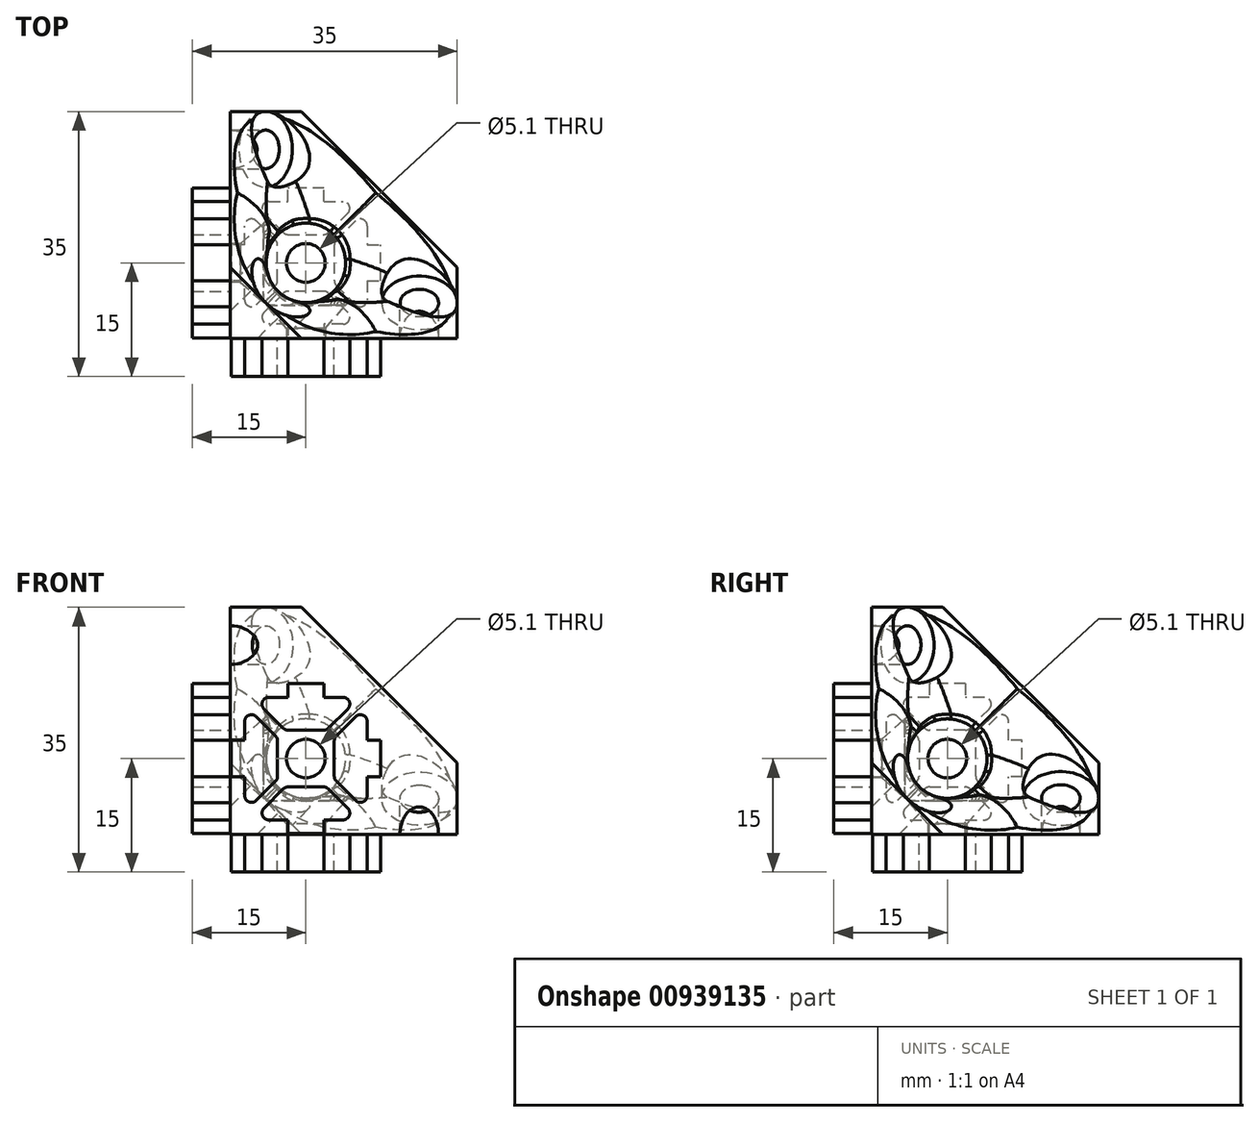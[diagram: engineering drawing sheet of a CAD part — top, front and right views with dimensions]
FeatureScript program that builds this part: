
annotation { "Feature Type Name" : "Feature", "Feature Type Description" : "" }
export const myFeature = defineFeature(function(context is Context, id is Id, definition is map)
    precondition{}
    {
        {
            var Q0;
            Q0=qCreatedBy(makeId("Front.planeOp"),FACE);
            var sketch = newSketch(context, id + "F0", { "sketchPlane" : qUnion([Q0])});
            skLineSegment(sketch, "E0.bottom", {"start": v(0, 0) * mm, "end": v(30, 0) * mm});
            skLineSegment(sketch, "E0.top", {"start": v(0, 30) * mm, "end": v(30, 30) * mm});
            skLineSegment(sketch, "E0.left", {"start": v(0, 0) * mm, "end": v(0, 30) * mm});
            skLineSegment(sketch, "E0.right", {"start": v(30, 0) * mm, "end": v(30, 30) * mm});
            skSolve(sketch);
        }
        {
            var Q0;
            Q0 = qSketchRegion(id + "F0", true);
            extrude(context, id + "F1", {"entities" : qUnion([Q0]), "oppositeDirection" : true, "depth" : 30 * mm, "offsetDistance" : 25 * mm});
        }
        {
            var Q0;
            Q0=makeQuery(id+"F1.opExtrude","CAP_FACE",FACE,{"disambiguationData":[OSD([sQuery(id+"F0.wireOp",EDGE,"E0.bottom"),sQuery(id+"F0.wireOp",EDGE,"E0.top"),sQuery(id+"F0.wireOp",EDGE,"E0.left"),sQuery(id+"F0.wireOp",EDGE,"E0.right")])],"isStart":true});
            var sketch = newSketch(context, id + "F2", { "sketchPlane" : qUnion([Q0])});
            skLineSegment(sketch, "E1", {"start": v(7.5, 20) * mm, "end": v(7.5, 18.2) * mm});
            skLineSegment(sketch, "E2", {"start": v(12.5, 20) * mm, "end": v(12.5, 18.2) * mm});
            skLineSegment(sketch, "E3", {"start": v(12.5, 18.2) * mm, "end": v(14.9, 18.2) * mm});
            skLineSegment(sketch, "E4", {"start": v(5.1, 18.2) * mm, "end": v(7.5, 18.2) * mm});
            skLineSegment(sketch, "E5", {"start": v(4.4, 16.5) * mm, "end": v(6.94, 13.94) * mm});
            skLineSegment(sketch, "E6", {"start": v(15.6, 16.5) * mm, "end": v(13.06, 13.94) * mm});
            skLineSegment(sketch, "E7", {"start": v(7.65, 13.65) * mm, "end": v(12.35, 13.65) * mm});
            skArc(sketch, "E8", {"start": v(12.35, 13.65) * mm, "mid": v(12.73, 13.73) * mm, "end": v(13.06, 13.94) * mm});
            skArc(sketch, "E9", {"start": v(6.94, 13.94) * mm, "mid": v(7.27, 13.73) * mm, "end": v(7.65, 13.65) * mm});
            skArc(sketch, "E10", {"start": v(5.1, 18.2) * mm, "mid": v(4.18, 17.58) * mm, "end": v(4.4, 16.5) * mm});
            skArc(sketch, "E11", {"start": v(15.6, 16.5) * mm, "mid": v(15.82, 17.58) * mm, "end": v(14.9, 18.2) * mm});
            skLineSegment(sketch, "E12", {"start": v(7.5, 20) * mm, "end": v(12.5, 20) * mm});
            skLineSegment(sketch, "E13.0", {"start": v(9.41, 30) * mm, "end": v(30, 9.41) * mm, "construction": true});
            skLineSegment(sketch, "E14", {"start": v(0, 30) * mm, "end": v(9.41, 30) * mm, "construction": true});
            skLineSegment(sketch, "E15", {"start": v(30, 0) * mm, "end": v(30, 9.41) * mm, "construction": true});
            skLineSegment(sketch, "E16.0", {"start": v(7.6, 19.9) * mm, "end": v(7.6, 18.1) * mm});
            skLineSegment(sketch, "E16.1", {"start": v(15.54, 16.56) * mm, "end": v(12.99, 14.01) * mm});
            skArc(sketch, "E16.2", {"start": v(15.54, 16.56) * mm, "mid": v(15.73, 17.54) * mm, "end": v(14.9, 18.1) * mm});
            skLineSegment(sketch, "E16.3", {"start": v(12.4, 18.1) * mm, "end": v(14.9, 18.1) * mm});
            skLineSegment(sketch, "E16.4", {"start": v(12.4, 19.9) * mm, "end": v(12.4, 18.1) * mm});
            skArc(sketch, "E16.5", {"start": v(12.35, 13.75) * mm, "mid": v(12.7, 13.82) * mm, "end": v(12.99, 14.01) * mm});
            skLineSegment(sketch, "E16.6", {"start": v(7.6, 19.9) * mm, "end": v(12.4, 19.9) * mm});
            skLineSegment(sketch, "E16.7", {"start": v(7.65, 13.75) * mm, "end": v(12.35, 13.75) * mm});
            skArc(sketch, "E16.8", {"start": v(7.01, 14.01) * mm, "mid": v(7.3, 13.82) * mm, "end": v(7.65, 13.75) * mm});
            skLineSegment(sketch, "E16.9", {"start": v(4.46, 16.56) * mm, "end": v(7.01, 14.01) * mm});
            skArc(sketch, "E16.10", {"start": v(5.1, 18.1) * mm, "mid": v(4.27, 17.54) * mm, "end": v(4.46, 16.56) * mm});
            skLineSegment(sketch, "E16.11", {"start": v(5.1, 18.1) * mm, "end": v(7.6, 18.1) * mm});
            skLineSegment(sketch, "E17.1.0", {"start": v(0.1, 7.6) * mm, "end": v(0.1, 12.4) * mm});
            skLineSegment(sketch, "E17.1.1", {"start": v(0.1, 7.6) * mm, "end": v(1.9, 7.6) * mm});
            skLineSegment(sketch, "E17.1.2", {"start": v(1.9, 5.1) * mm, "end": v(1.9, 7.6) * mm});
            skArc(sketch, "E17.1.3", {"start": v(1.9, 5.1) * mm, "mid": v(2.46, 4.27) * mm, "end": v(3.44, 4.46) * mm});
            skLineSegment(sketch, "E17.1.4", {"start": v(3.44, 4.46) * mm, "end": v(5.99, 7.01) * mm});
            skArc(sketch, "E17.1.5", {"start": v(5.99, 7.01) * mm, "mid": v(6.18, 7.3) * mm, "end": v(6.25, 7.65) * mm});
            skLineSegment(sketch, "E17.1.6", {"start": v(6.25, 7.65) * mm, "end": v(6.25, 12.35) * mm});
            skArc(sketch, "E17.1.7", {"start": v(6.25, 12.35) * mm, "mid": v(6.18, 12.7) * mm, "end": v(5.99, 12.99) * mm});
            skLineSegment(sketch, "E17.1.8", {"start": v(3.44, 15.54) * mm, "end": v(5.99, 12.99) * mm});
            skArc(sketch, "E17.1.9", {"start": v(3.44, 15.54) * mm, "mid": v(2.46, 15.73) * mm, "end": v(1.9, 14.9) * mm});
            skLineSegment(sketch, "E17.1.10", {"start": v(1.9, 12.4) * mm, "end": v(1.9, 14.9) * mm});
            skLineSegment(sketch, "E17.1.11", {"start": v(0.1, 12.4) * mm, "end": v(1.9, 12.4) * mm});
            skLineSegment(sketch, "E17.2.0", {"start": v(12.4, 0.1) * mm, "end": v(7.6, 0.1) * mm});
            skLineSegment(sketch, "E17.2.1", {"start": v(12.4, 0.1) * mm, "end": v(12.4, 1.9) * mm});
            skLineSegment(sketch, "E17.2.2", {"start": v(14.9, 1.9) * mm, "end": v(12.4, 1.9) * mm});
            skArc(sketch, "E17.2.3", {"start": v(14.9, 1.9) * mm, "mid": v(15.73, 2.46) * mm, "end": v(15.54, 3.44) * mm});
            skLineSegment(sketch, "E17.2.4", {"start": v(15.54, 3.44) * mm, "end": v(12.99, 5.99) * mm});
            skArc(sketch, "E17.2.5", {"start": v(12.99, 5.99) * mm, "mid": v(12.7, 6.18) * mm, "end": v(12.35, 6.25) * mm});
            skLineSegment(sketch, "E17.2.6", {"start": v(12.35, 6.25) * mm, "end": v(7.65, 6.25) * mm});
            skArc(sketch, "E17.2.7", {"start": v(7.65, 6.25) * mm, "mid": v(7.3, 6.18) * mm, "end": v(7.01, 5.99) * mm});
            skLineSegment(sketch, "E17.2.8", {"start": v(4.46, 3.44) * mm, "end": v(7.01, 5.99) * mm});
            skArc(sketch, "E17.2.9", {"start": v(4.46, 3.44) * mm, "mid": v(4.27, 2.46) * mm, "end": v(5.1, 1.9) * mm});
            skLineSegment(sketch, "E17.2.10", {"start": v(7.6, 1.9) * mm, "end": v(5.1, 1.9) * mm});
            skLineSegment(sketch, "E17.2.11", {"start": v(7.6, 0.1) * mm, "end": v(7.6, 1.9) * mm});
            skLineSegment(sketch, "E17.3.0", {"start": v(19.9, 12.4) * mm, "end": v(19.9, 7.6) * mm});
            skLineSegment(sketch, "E17.3.1", {"start": v(19.9, 12.4) * mm, "end": v(18.1, 12.4) * mm});
            skLineSegment(sketch, "E17.3.2", {"start": v(18.1, 14.9) * mm, "end": v(18.1, 12.4) * mm});
            skArc(sketch, "E17.3.3", {"start": v(18.1, 14.9) * mm, "mid": v(17.54, 15.73) * mm, "end": v(16.56, 15.54) * mm});
            skLineSegment(sketch, "E17.3.4", {"start": v(16.56, 15.54) * mm, "end": v(14.01, 12.99) * mm});
            skArc(sketch, "E17.3.5", {"start": v(14.01, 12.99) * mm, "mid": v(13.82, 12.7) * mm, "end": v(13.75, 12.35) * mm});
            skLineSegment(sketch, "E17.3.6", {"start": v(13.75, 12.35) * mm, "end": v(13.75, 7.65) * mm});
            skArc(sketch, "E17.3.7", {"start": v(13.75, 7.65) * mm, "mid": v(13.82, 7.3) * mm, "end": v(14.01, 7.01) * mm});
            skLineSegment(sketch, "E17.3.8", {"start": v(16.56, 4.46) * mm, "end": v(14.01, 7.01) * mm});
            skArc(sketch, "E17.3.9", {"start": v(16.56, 4.46) * mm, "mid": v(17.54, 4.27) * mm, "end": v(18.1, 5.1) * mm});
            skLineSegment(sketch, "E17.3.10", {"start": v(18.1, 7.6) * mm, "end": v(18.1, 5.1) * mm});
            skLineSegment(sketch, "E17.3.11", {"start": v(19.9, 7.6) * mm, "end": v(18.1, 7.6) * mm});
            skPoint(sketch, "E17.center", {"position": v(10, 10) * mm});
            skCircle(sketch, "E18", {"center": v(10, 10) * mm, "radius": 2.55 * mm});
            skLineSegment(sketch, "E19", {"start": v(0, 0) * mm, "end": v(0, 9.41) * mm, "construction": true});
            skLineSegment(sketch, "E20", {"start": v(0, 9.41) * mm, "end": v(9.41, 0.1) * mm, "construction": true});
            skLineSegment(sketch, "E21", {"start": v(9.41, 0.1) * mm, "end": v(0, 0) * mm, "construction": true});
            skSolve(sketch);
        }
        {
            var Q0;
            Q0=makeQuery(id+"F2.imprint","IMPRINT",FACE,{"disambiguationData":[TD([[makeQuery(id+"F2.imprint","IMPRINT",EDGE,{"derivedFrom":sQuery(id+"F2.wireOp",EDGE,"E16.0")}),1.0]])]});
            var Q1;
            Q1=makeQuery(id+"F2.imprint","IMPRINT",FACE,{"disambiguationData":[TD([[makeQuery(id+"F2.imprint","IMPRINT",EDGE,{"derivedFrom":sQuery(id+"F2.wireOp",EDGE,"E17.1.0")}),-1.0]])]});
            var Q2;
            Q2=makeQuery(id+"F2.imprint","IMPRINT",FACE,{"disambiguationData":[TD([[makeQuery(id+"F2.imprint","IMPRINT",EDGE,{"derivedFrom":sQuery(id+"F2.wireOp",EDGE,"E17.3.0")}),-1.0]])]});
            var Q3;
            Q3=makeQuery(id+"F2.imprint","IMPRINT",FACE,{"disambiguationData":[TD([[makeQuery(id+"F2.imprint","IMPRINT",EDGE,{"derivedFrom":sQuery(id+"F2.wireOp",EDGE,"E17.2.0")}),-1.0]])]});
            extrude(context, id + "F3", {"entities" : qUnion([Q0, Q1, Q2, Q3]), "operationType" : NewBodyOperationType.ADD, "depth" : 5 * mm, "offsetDistance" : 25 * mm});
        }
        {
            var Q0;
            Q0=makeQuery(id+"F2.imprint","IMPRINT",FACE,{"disambiguationData":[TD([[makeQuery(id+"F2.imprint","IMPRINT",EDGE,{"derivedFrom":sQuery(id+"F2.wireOp",EDGE,"E18")}),1.0]])]});
            extrude(context, id + "F4", {"entities" : qUnion([Q0]), "operationType" : NewBodyOperationType.REMOVE, "oppositeDirection" : true, "depth" : 1.35 * mm, "offsetDistance" : 25 * mm});
        }
        {
            var Q0;
            Q0=qCreatedBy(makeId("Front.planeOp"),FACE);
            cPlane(context, id + "F5", {"entities" : qUnion([Q0]), "cplaneType" : CPlaneType.OFFSET, "offset" : 4.4 * mm, "oppositeDirection" : true, "width" : 150 * mm, "height" : 150 * mm});
        }
        {
            var Q0;
            Q0=qCreatedBy(id+"F5.planeOp",FACE);
            var sketch = newSketch(context, id + "F6", { "sketchPlane" : qUnion([Q0])});
            skCircle(sketch, "E22", {"center": v(10, 10) * mm, "radius": 5.25 * mm});
            skSolve(sketch);
        }
        {
            var Q0;
            Q0 = qSketchRegion(id + "F6", true);
            extrude(context, id + "F7", {"entities" : qUnion([Q0]), "operationType" : NewBodyOperationType.REMOVE, "endBound" : BoundingType.THROUGH_ALL, "oppositeDirection" : true, "depth" : 25 * mm, "offsetDistance" : 25 * mm});
        }
        {
            var Q1;
            Q1=makeQuery(id+"F7.boolean.opBoolean","COPY",FACE,{"derivedFrom":makeQuery(id+"F7.opExtrude","CAP_FACE",FACE,{"disambiguationData":[OSD([sQuery(id+"F6.wireOp",EDGE,"E22")])],"isStart":true})});
            var Q2;
            Q2=makeQuery(id+"F4.boolean.opBoolean","COPY",FACE,{"derivedFrom":makeQuery(id+"F4.opExtrude","CAP_FACE",FACE,{"disambiguationData":[OSD([sQuery(id+"F2.wireOp",EDGE,"E18")])],"isStart":false})});
            loft(context, id + "F8", {"operationType" : NewBodyOperationType.REMOVE, "sheetProfilesArray" : [{ "sheetProfileEntities" : qUnion([Q1]) }, { "sheetProfileEntities" : qUnion([Q2]) }]});
        }
        {
            var Q0;
            Q0=makeQuery(id+"F1.opExtrude","SWEPT_FACE",FACE,{"disambiguationData":[OSD([sQuery(id+"F0.wireOp",EDGE,"E0.left")])]});
            var sketch = newSketch(context, id + "F9", { "sketchPlane" : qUnion([Q0])});
            skLineSegment(sketch, "E23.0", {"start": v(-9.41, 30) * mm, "end": v(-30, 9.41) * mm, "construction": true});
            skLineSegment(sketch, "E24", {"start": v(0, 30) * mm, "end": v(-9.41, 30) * mm, "construction": true});
            skLineSegment(sketch, "E25", {"start": v(-30, 9.41) * mm, "end": v(-30, 0) * mm, "construction": true});
            skCircle(sketch, "E26", {"center": v(-10, 10) * mm, "radius": 2.55 * mm});
            skLineSegment(sketch, "E27", {"start": v(0, 0) * mm, "end": v(-9.41, 0) * mm, "construction": true});
            skPoint(sketch, "E27.endSnap0", {"position": v(-9.41, 0.1) * mm});
            skLineSegment(sketch, "E28", {"start": v(-9.41, 0) * mm, "end": v(-0.09, 9.41) * mm, "construction": true});
            skLineSegment(sketch, "E29", {"start": v(-0.09, 9.41) * mm, "end": v(0, 0) * mm, "construction": true});
            skLineSegment(sketch, "E30", {"start": v(-12.5, 20) * mm, "end": v(-12.5, 18.2) * mm});
            skLineSegment(sketch, "E31", {"start": v(-7.5, 20) * mm, "end": v(-7.5, 18.2) * mm});
            skLineSegment(sketch, "E32", {"start": v(-7.5, 18.2) * mm, "end": v(-5.1, 18.2) * mm});
            skLineSegment(sketch, "E33", {"start": v(-14.9, 18.2) * mm, "end": v(-12.5, 18.2) * mm});
            skLineSegment(sketch, "E34", {"start": v(-15.6, 16.5) * mm, "end": v(-13.06, 13.94) * mm});
            skLineSegment(sketch, "E35", {"start": v(-4.4, 16.5) * mm, "end": v(-6.94, 13.94) * mm});
            skLineSegment(sketch, "E36", {"start": v(-12.35, 13.65) * mm, "end": v(-7.65, 13.65) * mm});
            skArc(sketch, "E37", {"start": v(-7.65, 13.65) * mm, "mid": v(-7.27, 13.73) * mm, "end": v(-6.94, 13.94) * mm});
            skArc(sketch, "E38", {"start": v(-13.06, 13.94) * mm, "mid": v(-12.73, 13.73) * mm, "end": v(-12.35, 13.65) * mm});
            skArc(sketch, "E39", {"start": v(-14.9, 18.2) * mm, "mid": v(-15.82, 17.58) * mm, "end": v(-15.6, 16.5) * mm});
            skArc(sketch, "E40", {"start": v(-4.4, 16.5) * mm, "mid": v(-4.18, 17.58) * mm, "end": v(-5.1, 18.2) * mm});
            skLineSegment(sketch, "E41", {"start": v(-12.5, 20) * mm, "end": v(-7.5, 20) * mm});
            skLineSegment(sketch, "E42.0", {"start": v(-12.4, 19.9) * mm, "end": v(-12.4, 18.1) * mm});
            skLineSegment(sketch, "E42.1", {"start": v(-4.46, 16.56) * mm, "end": v(-7.01, 14.01) * mm});
            skArc(sketch, "E42.2", {"start": v(-4.46, 16.56) * mm, "mid": v(-4.27, 17.54) * mm, "end": v(-5.1, 18.1) * mm});
            skLineSegment(sketch, "E42.3", {"start": v(-7.6, 18.1) * mm, "end": v(-5.1, 18.1) * mm});
            skLineSegment(sketch, "E42.4", {"start": v(-7.6, 19.9) * mm, "end": v(-7.6, 18.1) * mm});
            skArc(sketch, "E42.5", {"start": v(-7.65, 13.75) * mm, "mid": v(-7.3, 13.82) * mm, "end": v(-7.01, 14.01) * mm});
            skLineSegment(sketch, "E42.6", {"start": v(-12.4, 19.9) * mm, "end": v(-7.6, 19.9) * mm});
            skLineSegment(sketch, "E42.7", {"start": v(-12.35, 13.75) * mm, "end": v(-7.65, 13.75) * mm});
            skArc(sketch, "E42.8", {"start": v(-12.99, 14.01) * mm, "mid": v(-12.7, 13.82) * mm, "end": v(-12.35, 13.75) * mm});
            skLineSegment(sketch, "E42.9", {"start": v(-15.54, 16.56) * mm, "end": v(-12.99, 14.01) * mm});
            skArc(sketch, "E42.10", {"start": v(-14.9, 18.1) * mm, "mid": v(-15.73, 17.54) * mm, "end": v(-15.54, 16.56) * mm});
            skLineSegment(sketch, "E42.11", {"start": v(-14.9, 18.1) * mm, "end": v(-12.4, 18.1) * mm});
            skLineSegment(sketch, "E43.1.0", {"start": v(-19.9, 7.6) * mm, "end": v(-19.9, 12.4) * mm});
            skLineSegment(sketch, "E43.1.1", {"start": v(-19.9, 7.6) * mm, "end": v(-18.1, 7.6) * mm});
            skLineSegment(sketch, "E43.1.2", {"start": v(-18.1, 5.1) * mm, "end": v(-18.1, 7.6) * mm});
            skArc(sketch, "E43.1.3", {"start": v(-18.1, 5.1) * mm, "mid": v(-17.54, 4.27) * mm, "end": v(-16.56, 4.46) * mm});
            skLineSegment(sketch, "E43.1.4", {"start": v(-16.56, 4.46) * mm, "end": v(-14.01, 7.01) * mm});
            skArc(sketch, "E43.1.5", {"start": v(-14.01, 7.01) * mm, "mid": v(-13.82, 7.3) * mm, "end": v(-13.75, 7.65) * mm});
            skLineSegment(sketch, "E43.1.6", {"start": v(-13.75, 7.65) * mm, "end": v(-13.75, 12.35) * mm});
            skArc(sketch, "E43.1.7", {"start": v(-13.75, 12.35) * mm, "mid": v(-13.82, 12.7) * mm, "end": v(-14.01, 12.99) * mm});
            skLineSegment(sketch, "E43.1.8", {"start": v(-16.56, 15.54) * mm, "end": v(-14.01, 12.99) * mm});
            skArc(sketch, "E43.1.9", {"start": v(-16.56, 15.54) * mm, "mid": v(-17.54, 15.73) * mm, "end": v(-18.1, 14.9) * mm});
            skLineSegment(sketch, "E43.1.10", {"start": v(-18.1, 12.4) * mm, "end": v(-18.1, 14.9) * mm});
            skLineSegment(sketch, "E43.1.11", {"start": v(-19.9, 12.4) * mm, "end": v(-18.1, 12.4) * mm});
            skLineSegment(sketch, "E43.2.0", {"start": v(-7.6, 0.1) * mm, "end": v(-12.4, 0.1) * mm});
            skLineSegment(sketch, "E43.2.1", {"start": v(-7.6, 0.1) * mm, "end": v(-7.6, 1.9) * mm});
            skLineSegment(sketch, "E43.2.2", {"start": v(-5.1, 1.9) * mm, "end": v(-7.6, 1.9) * mm});
            skArc(sketch, "E43.2.3", {"start": v(-5.1, 1.9) * mm, "mid": v(-4.27, 2.46) * mm, "end": v(-4.46, 3.44) * mm});
            skLineSegment(sketch, "E43.2.4", {"start": v(-4.46, 3.44) * mm, "end": v(-7.01, 5.99) * mm});
            skArc(sketch, "E43.2.5", {"start": v(-7.01, 5.99) * mm, "mid": v(-7.3, 6.18) * mm, "end": v(-7.65, 6.25) * mm});
            skLineSegment(sketch, "E43.2.6", {"start": v(-7.65, 6.25) * mm, "end": v(-12.35, 6.25) * mm});
            skArc(sketch, "E43.2.7", {"start": v(-12.35, 6.25) * mm, "mid": v(-12.7, 6.18) * mm, "end": v(-12.99, 5.99) * mm});
            skLineSegment(sketch, "E43.2.8", {"start": v(-15.54, 3.44) * mm, "end": v(-12.99, 5.99) * mm});
            skArc(sketch, "E43.2.9", {"start": v(-15.54, 3.44) * mm, "mid": v(-15.73, 2.46) * mm, "end": v(-14.9, 1.9) * mm});
            skLineSegment(sketch, "E43.2.10", {"start": v(-12.4, 1.9) * mm, "end": v(-14.9, 1.9) * mm});
            skLineSegment(sketch, "E43.2.11", {"start": v(-12.4, 0.1) * mm, "end": v(-12.4, 1.9) * mm});
            skLineSegment(sketch, "E43.3.0", {"start": v(-0.1, 12.4) * mm, "end": v(-0.1, 7.6) * mm});
            skLineSegment(sketch, "E43.3.1", {"start": v(-0.1, 12.4) * mm, "end": v(-1.9, 12.4) * mm});
            skLineSegment(sketch, "E43.3.2", {"start": v(-1.9, 14.9) * mm, "end": v(-1.9, 12.4) * mm});
            skArc(sketch, "E43.3.3", {"start": v(-1.9, 14.9) * mm, "mid": v(-2.46, 15.73) * mm, "end": v(-3.44, 15.54) * mm});
            skLineSegment(sketch, "E43.3.4", {"start": v(-3.44, 15.54) * mm, "end": v(-5.99, 12.99) * mm});
            skArc(sketch, "E43.3.5", {"start": v(-5.99, 12.99) * mm, "mid": v(-6.18, 12.7) * mm, "end": v(-6.25, 12.35) * mm});
            skLineSegment(sketch, "E43.3.6", {"start": v(-6.25, 12.35) * mm, "end": v(-6.25, 7.65) * mm});
            skArc(sketch, "E43.3.7", {"start": v(-6.25, 7.65) * mm, "mid": v(-6.18, 7.3) * mm, "end": v(-5.99, 7.01) * mm});
            skLineSegment(sketch, "E43.3.8", {"start": v(-3.44, 4.46) * mm, "end": v(-5.99, 7.01) * mm});
            skArc(sketch, "E43.3.9", {"start": v(-3.44, 4.46) * mm, "mid": v(-2.46, 4.27) * mm, "end": v(-1.9, 5.1) * mm});
            skLineSegment(sketch, "E43.3.10", {"start": v(-1.9, 7.6) * mm, "end": v(-1.9, 5.1) * mm});
            skLineSegment(sketch, "E43.3.11", {"start": v(-0.1, 7.6) * mm, "end": v(-1.9, 7.6) * mm});
            skSolve(sketch);
        }
        {
            var Q0;
            Q0=makeQuery(id+"F9.imprint","IMPRINT",FACE,{"disambiguationData":[TD([[makeQuery(id+"F9.imprint","IMPRINT",EDGE,{"derivedFrom":sQuery(id+"F9.wireOp",EDGE,"E42.0")}),1.0]])]});
            var Q1;
            Q1=makeQuery(id+"F9.imprint","IMPRINT",FACE,{"disambiguationData":[TD([[makeQuery(id+"F9.imprint","IMPRINT",EDGE,{"derivedFrom":sQuery(id+"F9.wireOp",EDGE,"E43.1.0")}),-1.0]])]});
            var Q2;
            Q2=makeQuery(id+"F9.imprint","IMPRINT",FACE,{"disambiguationData":[TD([[makeQuery(id+"F9.imprint","IMPRINT",EDGE,{"derivedFrom":sQuery(id+"F9.wireOp",EDGE,"E43.2.0")}),-1.0]])]});
            var Q3;
            Q3=makeQuery(id+"F9.imprint","IMPRINT",FACE,{"disambiguationData":[TD([[makeQuery(id+"F9.imprint","IMPRINT",EDGE,{"derivedFrom":sQuery(id+"F9.wireOp",EDGE,"E43.3.0")}),-1.0]])]});
            extrude(context, id + "F10", {"entities" : qUnion([Q0, Q1, Q2, Q3]), "operationType" : NewBodyOperationType.ADD, "depth" : 5 * mm, "offsetDistance" : 25 * mm});
        }
        {
            var Q0;
            Q0=makeQuery(id+"F9.imprint","IMPRINT",FACE,{"disambiguationData":[TD([[makeQuery(id+"F9.imprint","IMPRINT",EDGE,{"derivedFrom":sQuery(id+"F9.wireOp",EDGE,"E26")}),1.0]])]});
            extrude(context, id + "F11", {"entities" : qUnion([Q0]), "operationType" : NewBodyOperationType.REMOVE, "oppositeDirection" : true, "depth" : 1.35 * mm, "offsetDistance" : 25 * mm});
        }
        {
            var Q0;
            Q0=qCreatedBy(makeId("Right.planeOp"),FACE);
            cPlane(context, id + "F12", {"entities" : qUnion([Q0]), "cplaneType" : CPlaneType.OFFSET, "offset" : 4.4 * mm, "width" : 150 * mm, "height" : 150 * mm});
        }
        {
            var Q0;
            Q0=qCreatedBy(id+"F12.planeOp",FACE);
            var sketch = newSketch(context, id + "F13", { "sketchPlane" : qUnion([Q0])});
            skCircle(sketch, "E44", {"center": v(10, 10) * mm, "radius": 5.25 * mm});
            skSolve(sketch);
        }
        {
            var Q0;
            Q0 = qSketchRegion(id + "F13", true);
            var Q1;
            Q1=makeQuery(id+"F1.opExtrude","SWEPT_FACE",FACE,{"disambiguationData":[OSD([sQuery(id+"F0.wireOp",EDGE,"E0.right")])]});
            extrude(context, id + "F14", {"entities" : qUnion([Q0]), "operationType" : NewBodyOperationType.REMOVE, "endBound" : BoundingType.UP_TO_SURFACE, "depth" : 25 * mm, "endBoundEntityFace" : qUnion([Q1]), "offsetDistance" : 25 * mm});
        }
        {
            var Q1;
            Q1=makeQuery(id+"F11.boolean.opBoolean","COPY",FACE,{"derivedFrom":makeQuery(id+"F11.opExtrude","CAP_FACE",FACE,{"disambiguationData":[OSD([sQuery(id+"F9.wireOp",EDGE,"E26")])],"isStart":false})});
            var Q2;
            Q2=makeQuery(id+"F14.boolean.opBoolean","COPY",FACE,{"derivedFrom":makeQuery(id+"F14.opExtrude","CAP_FACE",FACE,{"disambiguationData":[OSD([sQuery(id+"F13.wireOp",EDGE,"E44")])],"isStart":true})});
            loft(context, id + "F15", {"operationType" : NewBodyOperationType.REMOVE, "sheetProfilesArray" : [{ "sheetProfileEntities" : qUnion([Q1]) }, { "sheetProfileEntities" : qUnion([Q2]) }]});
        }
        {
            var Q0;
            Q0=makeQuery(id+"F1.opExtrude","SWEPT_FACE",FACE,{"disambiguationData":[OSD([sQuery(id+"F0.wireOp",EDGE,"E0.bottom")])]});
            var sketch = newSketch(context, id + "F16", { "sketchPlane" : qUnion([Q0])});
            skLineSegment(sketch, "E45", {"start": v(18.2, -7.5) * mm, "end": v(20, -7.5) * mm});
            skLineSegment(sketch, "E46", {"start": v(18.2, -12.5) * mm, "end": v(20, -12.5) * mm});
            skLineSegment(sketch, "E47", {"start": v(18.2, -14.9) * mm, "end": v(18.2, -12.5) * mm});
            skLineSegment(sketch, "E48", {"start": v(18.2, -7.5) * mm, "end": v(18.2, -5.1) * mm});
            skLineSegment(sketch, "E49", {"start": v(13.94, -13.06) * mm, "end": v(16.5, -15.6) * mm});
            skLineSegment(sketch, "E50", {"start": v(13.94, -6.94) * mm, "end": v(16.5, -4.4) * mm});
            skLineSegment(sketch, "E51", {"start": v(13.65, -12.35) * mm, "end": v(13.65, -7.65) * mm});
            skArc(sketch, "E52", {"start": v(13.65, -12.35) * mm, "mid": v(13.73, -12.73) * mm, "end": v(13.94, -13.06) * mm});
            skArc(sketch, "E53", {"start": v(13.94, -6.94) * mm, "mid": v(13.73, -7.27) * mm, "end": v(13.65, -7.65) * mm});
            skArc(sketch, "E54", {"start": v(18.2, -5.1) * mm, "mid": v(17.58, -4.18) * mm, "end": v(16.5, -4.4) * mm});
            skArc(sketch, "E55", {"start": v(16.5, -15.6) * mm, "mid": v(17.58, -15.82) * mm, "end": v(18.2, -14.9) * mm});
            skLineSegment(sketch, "E56", {"start": v(20, -7.5) * mm, "end": v(20, -12.5) * mm});
            skLineSegment(sketch, "E57.0", {"start": v(9.41, -30) * mm, "end": v(30, -9.41) * mm, "construction": true});
            skLineSegment(sketch, "E58", {"start": v(30, 0) * mm, "end": v(30, -30) * mm, "construction": true});
            skLineSegment(sketch, "E59", {"start": v(30, -30) * mm, "end": v(0, -30) * mm, "construction": true});
            skCircle(sketch, "E60", {"center": v(10, -10) * mm, "radius": 2.55 * mm});
            skLineSegment(sketch, "E61.0", {"start": v(18.1, -7.6) * mm, "end": v(19.9, -7.6) * mm});
            skLineSegment(sketch, "E61.1", {"start": v(14.01, -12.99) * mm, "end": v(16.56, -15.54) * mm});
            skArc(sketch, "E61.2", {"start": v(16.56, -15.54) * mm, "mid": v(17.54, -15.73) * mm, "end": v(18.1, -14.9) * mm});
            skLineSegment(sketch, "E61.3", {"start": v(18.1, -14.9) * mm, "end": v(18.1, -12.4) * mm});
            skLineSegment(sketch, "E61.4", {"start": v(18.1, -12.4) * mm, "end": v(19.9, -12.4) * mm});
            skArc(sketch, "E61.5", {"start": v(13.75, -12.35) * mm, "mid": v(13.82, -12.7) * mm, "end": v(14.01, -12.99) * mm});
            skLineSegment(sketch, "E61.6", {"start": v(19.9, -7.6) * mm, "end": v(19.9, -12.4) * mm});
            skLineSegment(sketch, "E61.7", {"start": v(13.75, -12.35) * mm, "end": v(13.75, -7.65) * mm});
            skArc(sketch, "E61.8", {"start": v(14.01, -7.01) * mm, "mid": v(13.82, -7.3) * mm, "end": v(13.75, -7.65) * mm});
            skLineSegment(sketch, "E61.9", {"start": v(14.01, -7.01) * mm, "end": v(16.56, -4.46) * mm});
            skArc(sketch, "E61.10", {"start": v(18.1, -5.1) * mm, "mid": v(17.54, -4.27) * mm, "end": v(16.56, -4.46) * mm});
            skLineSegment(sketch, "E61.11", {"start": v(18.1, -7.6) * mm, "end": v(18.1, -5.1) * mm});
            skLineSegment(sketch, "E62.1.0", {"start": v(7.6, -0.1) * mm, "end": v(12.4, -0.1) * mm});
            skLineSegment(sketch, "E62.1.1", {"start": v(7.6, -1.9) * mm, "end": v(7.6, -0.1) * mm});
            skLineSegment(sketch, "E62.1.2", {"start": v(7.6, -1.9) * mm, "end": v(5.1, -1.9) * mm});
            skArc(sketch, "E62.1.3", {"start": v(5.1, -1.9) * mm, "mid": v(4.27, -2.46) * mm, "end": v(4.46, -3.44) * mm});
            skLineSegment(sketch, "E62.1.4", {"start": v(7.01, -5.99) * mm, "end": v(4.46, -3.44) * mm});
            skArc(sketch, "E62.1.5", {"start": v(7.01, -5.99) * mm, "mid": v(7.3, -6.18) * mm, "end": v(7.65, -6.25) * mm});
            skLineSegment(sketch, "E62.1.6", {"start": v(12.35, -6.25) * mm, "end": v(7.65, -6.25) * mm});
            skArc(sketch, "E62.1.7", {"start": v(12.35, -6.25) * mm, "mid": v(12.7, -6.18) * mm, "end": v(12.99, -5.99) * mm});
            skLineSegment(sketch, "E62.1.8", {"start": v(12.99, -5.99) * mm, "end": v(15.54, -3.44) * mm});
            skArc(sketch, "E62.1.9", {"start": v(15.54, -3.44) * mm, "mid": v(15.73, -2.46) * mm, "end": v(14.9, -1.9) * mm});
            skLineSegment(sketch, "E62.1.10", {"start": v(14.9, -1.9) * mm, "end": v(12.4, -1.9) * mm});
            skLineSegment(sketch, "E62.1.11", {"start": v(12.4, -1.9) * mm, "end": v(12.4, -0.1) * mm});
            skLineSegment(sketch, "E62.2.0", {"start": v(0.1, -12.4) * mm, "end": v(0.1, -7.6) * mm});
            skLineSegment(sketch, "E62.2.1", {"start": v(1.9, -12.4) * mm, "end": v(0.1, -12.4) * mm});
            skLineSegment(sketch, "E62.2.2", {"start": v(1.9, -12.4) * mm, "end": v(1.9, -14.9) * mm});
            skArc(sketch, "E62.2.3", {"start": v(1.9, -14.9) * mm, "mid": v(2.46, -15.73) * mm, "end": v(3.44, -15.54) * mm});
            skLineSegment(sketch, "E62.2.4", {"start": v(5.99, -12.99) * mm, "end": v(3.44, -15.54) * mm});
            skArc(sketch, "E62.2.5", {"start": v(5.99, -12.99) * mm, "mid": v(6.18, -12.7) * mm, "end": v(6.25, -12.35) * mm});
            skLineSegment(sketch, "E62.2.6", {"start": v(6.25, -7.65) * mm, "end": v(6.25, -12.35) * mm});
            skArc(sketch, "E62.2.7", {"start": v(6.25, -7.65) * mm, "mid": v(6.18, -7.3) * mm, "end": v(5.99, -7.01) * mm});
            skLineSegment(sketch, "E62.2.8", {"start": v(5.99, -7.01) * mm, "end": v(3.44, -4.46) * mm});
            skArc(sketch, "E62.2.9", {"start": v(3.44, -4.46) * mm, "mid": v(2.46, -4.27) * mm, "end": v(1.9, -5.1) * mm});
            skLineSegment(sketch, "E62.2.10", {"start": v(1.9, -5.1) * mm, "end": v(1.9, -7.6) * mm});
            skLineSegment(sketch, "E62.2.11", {"start": v(1.9, -7.6) * mm, "end": v(0.1, -7.6) * mm});
            skLineSegment(sketch, "E62.3.0", {"start": v(12.4, -19.9) * mm, "end": v(7.6, -19.9) * mm});
            skLineSegment(sketch, "E62.3.1", {"start": v(12.4, -18.1) * mm, "end": v(12.4, -19.9) * mm});
            skLineSegment(sketch, "E62.3.2", {"start": v(12.4, -18.1) * mm, "end": v(14.9, -18.1) * mm});
            skArc(sketch, "E62.3.3", {"start": v(14.9, -18.1) * mm, "mid": v(15.73, -17.54) * mm, "end": v(15.54, -16.56) * mm});
            skLineSegment(sketch, "E62.3.4", {"start": v(12.99, -14.01) * mm, "end": v(15.54, -16.56) * mm});
            skArc(sketch, "E62.3.5", {"start": v(12.99, -14.01) * mm, "mid": v(12.7, -13.82) * mm, "end": v(12.35, -13.75) * mm});
            skLineSegment(sketch, "E62.3.6", {"start": v(7.65, -13.75) * mm, "end": v(12.35, -13.75) * mm});
            skArc(sketch, "E62.3.7", {"start": v(7.65, -13.75) * mm, "mid": v(7.3, -13.82) * mm, "end": v(7.01, -14.01) * mm});
            skLineSegment(sketch, "E62.3.8", {"start": v(7.01, -14.01) * mm, "end": v(4.46, -16.56) * mm});
            skArc(sketch, "E62.3.9", {"start": v(4.46, -16.56) * mm, "mid": v(4.27, -17.54) * mm, "end": v(5.1, -18.1) * mm});
            skLineSegment(sketch, "E62.3.10", {"start": v(5.1, -18.1) * mm, "end": v(7.6, -18.1) * mm});
            skLineSegment(sketch, "E62.3.11", {"start": v(7.6, -18.1) * mm, "end": v(7.6, -19.9) * mm});
            skPoint(sketch, "E63", {"position": v(9.41, 0) * mm});
            skSolve(sketch);
        }
        {
            var Q0;
            Q0=makeQuery(id+"F16.imprint","IMPRINT",FACE,{"disambiguationData":[TD([[makeQuery(id+"F16.imprint","IMPRINT",EDGE,{"derivedFrom":sQuery(id+"F16.wireOp",EDGE,"E61.0")}),-1.0]])]});
            var Q1;
            Q1=makeQuery(id+"F16.imprint","IMPRINT",FACE,{"disambiguationData":[TD([[makeQuery(id+"F16.imprint","IMPRINT",EDGE,{"derivedFrom":sQuery(id+"F16.wireOp",EDGE,"E62.1.0")}),-1.0]])]});
            var Q2;
            Q2=makeQuery(id+"F16.imprint","IMPRINT",FACE,{"disambiguationData":[TD([[makeQuery(id+"F16.imprint","IMPRINT",EDGE,{"derivedFrom":sQuery(id+"F16.wireOp",EDGE,"E62.3.0")}),-1.0]])]});
            var Q3;
            Q3=makeQuery(id+"F16.imprint","IMPRINT",FACE,{"disambiguationData":[TD([[makeQuery(id+"F16.imprint","IMPRINT",EDGE,{"derivedFrom":sQuery(id+"F16.wireOp",EDGE,"E62.2.0")}),-1.0]])]});
            extrude(context, id + "F17", {"entities" : qUnion([Q0, Q1, Q2, Q3]), "operationType" : NewBodyOperationType.ADD, "depth" : 5 * mm, "offsetDistance" : 25 * mm});
        }
        {
            var Q0;
            Q0=makeQuery(id+"F16.imprint","IMPRINT",FACE,{"disambiguationData":[TD([[makeQuery(id+"F16.imprint","IMPRINT",EDGE,{"derivedFrom":sQuery(id+"F16.wireOp",EDGE,"E60")}),1.0]])]});
            extrude(context, id + "F18", {"entities" : qUnion([Q0]), "operationType" : NewBodyOperationType.REMOVE, "oppositeDirection" : true, "depth" : 1.35 * mm, "offsetDistance" : 25 * mm});
        }
        {
            var Q0;
            Q0=qCreatedBy(makeId("Top.planeOp"),FACE);
            cPlane(context, id + "F19", {"entities" : qUnion([Q0]), "cplaneType" : CPlaneType.OFFSET, "offset" : 4.4 * mm, "width" : 150 * mm, "height" : 150 * mm});
        }
        {
            var Q0;
            Q0=qCreatedBy(id+"F19.planeOp",FACE);
            var sketch = newSketch(context, id + "F20", { "sketchPlane" : qUnion([Q0])});
            skCircle(sketch, "E64", {"center": v(10, 10) * mm, "radius": 5.25 * mm});
            skSolve(sketch);
        }
        {
            var Q0;
            Q0 = qSketchRegion(id + "F20", true);
            var Q1;
            Q1=makeQuery(id+"F1.opExtrude","SWEPT_FACE",FACE,{"disambiguationData":[OSD([sQuery(id+"F0.wireOp",EDGE,"E0.top")])]});
            extrude(context, id + "F21", {"entities" : qUnion([Q0]), "operationType" : NewBodyOperationType.REMOVE, "endBound" : BoundingType.UP_TO_SURFACE, "depth" : 25 * mm, "endBoundEntityFace" : qUnion([Q1]), "offsetDistance" : 25 * mm});
        }
        {
            var Q1;
            Q1=makeQuery(id+"F18.boolean.opBoolean","COPY",FACE,{"derivedFrom":makeQuery(id+"F18.opExtrude","CAP_FACE",FACE,{"disambiguationData":[OSD([sQuery(id+"F16.wireOp",EDGE,"E60")])],"isStart":false})});
            var Q2;
            Q2=makeQuery(id+"F21.boolean.opBoolean","COPY",FACE,{"derivedFrom":makeQuery(id+"F21.opExtrude","CAP_FACE",FACE,{"disambiguationData":[OSD([sQuery(id+"F20.wireOp",EDGE,"E64")])],"isStart":true})});
            loft(context, id + "F22", {"operationType" : NewBodyOperationType.REMOVE, "sheetProfilesArray" : [{ "sheetProfileEntities" : qUnion([Q1]) }, { "sheetProfileEntities" : qUnion([Q2]) }]});
        }
        {
            var Q0;
            Q0=sQuery(id+"F2.wireOp",VERTEX,"E13.0.start");
            var Q1;
            Q1=sQuery(id+"F9.wireOp",VERTEX,"E23.0.start");
            var Q2;
            Q2=sQuery(id+"F9.wireOp",VERTEX,"E23.0.end");
            cPlane(context, id + "F23", {"entities" : qUnion([Q0, Q1, Q2]), "cplaneType" : CPlaneType.THREE_POINT, "offset" : 25 * mm, "width" : 150 * mm, "height" : 150 * mm});
        }
        {
            var Q0;
            Q0=qCreatedBy(id+"F23.planeOp",FACE);
            var sketch = newSketch(context, id + "F24", { "sketchPlane" : qUnion([Q0])});
            skLineSegment(sketch, "E65", {"start": v(4.56, 21.21) * mm, "end": v(16.1, 14.56) * mm});
            skLineSegment(sketch, "E66", {"start": v(16.1, 14.56) * mm, "end": v(16.1, -14.56) * mm});
            skLineSegment(sketch, "E67", {"start": v(16.1, -14.56) * mm, "end": v(4.56, -21.21) * mm});
            skLineSegment(sketch, "E68", {"start": v(4.56, -21.21) * mm, "end": v(-20.65, -6.66) * mm});
            skLineSegment(sketch, "E69", {"start": v(-20.65, -6.66) * mm, "end": v(-20.65, 6.66) * mm});
            skLineSegment(sketch, "E70", {"start": v(-20.65, 6.66) * mm, "end": v(4.56, 21.21) * mm});
            skSolve(sketch);
        }
        {
            var Q0;
            Q0 = qSketchRegion(id + "F24", true);
            var Q1;
            Q1=makeQuery(id+"F1.opExtrude","CAP_VERTEX",VERTEX,{"disambiguationData":[OSD([sQuery(id+"F0.wireOp",EDGE,"E0.top"),sQuery(id+"F0.wireOp",EDGE,"E0.right")])],"isStart":false});
            extrude(context, id + "F25", {"entities" : qUnion([Q0]), "operationType" : NewBodyOperationType.REMOVE, "endBound" : BoundingType.UP_TO_VERTEX, "depth" : 25 * mm, "endBoundEntityVertex" : qUnion([Q1]), "offsetDistance" : 25 * mm});
        }
        {
            var Q0;
            Q0=makeQuery(id+"F25.boolean.opBoolean","COPY",FACE,{"derivedFrom":makeQuery(id+"F25.opExtrude","SWEPT_FACE",FACE,{"disambiguationData":[OSD([sQuery(id+"F24.wireOp",EDGE,"E70")])]})});
            var Q1;
            Q1=makeQuery(id+"F1.opExtrude","CAP_VERTEX",VERTEX,{"disambiguationData":[OSD([sQuery(id+"F0.wireOp",EDGE,"E0.top"),sQuery(id+"F0.wireOp",EDGE,"E0.right")])],"isStart":true});
            extrude(context, id + "F26", {"entities" : qUnion([Q0]), "operationType" : NewBodyOperationType.REMOVE, "endBound" : BoundingType.UP_TO_VERTEX, "oppositeDirection" : true, "depth" : 25 * mm, "endBoundEntityVertex" : qUnion([Q1]), "offsetDistance" : 25 * mm});
        }
        {
            var Q0;
            Q0=makeQuery(id+"F25.boolean.opBoolean","COPY",FACE,{"derivedFrom":makeQuery(id+"F25.opExtrude","SWEPT_FACE",FACE,{"disambiguationData":[OSD([sQuery(id+"F24.wireOp",EDGE,"E66")])]})});
            var Q1;
            Q1=makeQuery(id+"F1.opExtrude","CAP_VERTEX",VERTEX,{"disambiguationData":[OSD([sQuery(id+"F0.wireOp",EDGE,"E0.top"),sQuery(id+"F0.wireOp",EDGE,"E0.left")])],"isStart":false});
            extrude(context, id + "F27", {"entities" : qUnion([Q0]), "operationType" : NewBodyOperationType.REMOVE, "endBound" : BoundingType.UP_TO_VERTEX, "oppositeDirection" : true, "depth" : 25 * mm, "endBoundEntityVertex" : qUnion([Q1]), "offsetDistance" : 25 * mm});
        }
        {
            var Q0;
            Q0=makeQuery(id+"F25.boolean.opBoolean","COPY",FACE,{"derivedFrom":makeQuery(id+"F25.opExtrude","SWEPT_FACE",FACE,{"disambiguationData":[OSD([sQuery(id+"F24.wireOp",EDGE,"E68")])]})});
            var Q1;
            Q1=sQuery(id+"F16.wireOp",VERTEX,"E58.end");
            extrude(context, id + "F28", {"entities" : qUnion([Q0]), "operationType" : NewBodyOperationType.REMOVE, "endBound" : BoundingType.UP_TO_VERTEX, "oppositeDirection" : true, "depth" : 25 * mm, "endBoundEntityVertex" : qUnion([Q1]), "offsetDistance" : 25 * mm});
        }
        {
            var Q0;
            Q0=sQuery(id+"F2.wireOp",VERTEX,"E19.end");
            var Q1;
            {var subQ1=sQuery(id+"F24.wireOp",EDGE,"E67");var subQ2=sQuery(id+"F24.wireOp",EDGE,"E66");Q1=makeQuery(id+"F25.boolean.opBoolean","COPY",VERTEX,{"disambiguationData":[TD([makeQuery(id+"F25.opExtrude","CAP_FACE",FACE,{"disambiguationData":[OSD([sQuery(id+"F24.wireOp",EDGE,"E65"),subQ2,subQ1,sQuery(id+"F24.wireOp",EDGE,"E68"),sQuery(id+"F24.wireOp",EDGE,"E69"),sQuery(id+"F24.wireOp",EDGE,"E70")])],"isStart":true})])],"derivedFrom":makeQuery(id+"F25.opExtrude","CAP_VERTEX",VERTEX,{"disambiguationData":[OSD([subQ2,subQ1])],"isStart":true})});}
            var Q2;
            {var subQ1=sQuery(id+"F24.wireOp",EDGE,"E68");var subQ2=sQuery(id+"F24.wireOp",EDGE,"E67");Q2=makeQuery(id+"F25.boolean.opBoolean","COPY",VERTEX,{"disambiguationData":[TD([makeQuery(id+"F25.opExtrude","CAP_FACE",FACE,{"disambiguationData":[OSD([sQuery(id+"F24.wireOp",EDGE,"E65"),sQuery(id+"F24.wireOp",EDGE,"E66"),subQ2,subQ1,sQuery(id+"F24.wireOp",EDGE,"E69"),sQuery(id+"F24.wireOp",EDGE,"E70")])],"isStart":true})])],"derivedFrom":makeQuery(id+"F25.opExtrude","CAP_VERTEX",VERTEX,{"disambiguationData":[OSD([subQ2,subQ1])],"isStart":true})});}
            cPlane(context, id + "F29", {"entities" : qUnion([Q0, Q1, Q2]), "cplaneType" : CPlaneType.THREE_POINT, "offset" : 25 * mm, "width" : 150 * mm, "height" : 150 * mm});
        }
        {
            var Q0;
            Q0=qCreatedBy(id+"F29.planeOp",FACE);
            var sketch = newSketch(context, id + "F30", { "sketchPlane" : qUnion([Q0])});
            skCircle(sketch, "E71", {"center": v(-0.05, 25) * mm, "radius": 2.55 * mm});
            skSolve(sketch);
        }
        {
            var Q0;
            Q0 = qSketchRegion(id + "F30", true);
            var Q1;
            Q1=makeQuery(id+"F1.opExtrude","CAP_VERTEX",VERTEX,{"disambiguationData":[OSD([sQuery(id+"F0.wireOp",EDGE,"E0.bottom"),sQuery(id+"F0.wireOp",EDGE,"E0.left")])],"isStart":false});
            extrude(context, id + "F31", {"entities" : qUnion([Q0]), "operationType" : NewBodyOperationType.REMOVE, "endBound" : BoundingType.UP_TO_VERTEX, "oppositeDirection" : true, "depth" : 25 * mm, "endBoundEntityVertex" : qUnion([Q1]), "offsetDistance" : 25 * mm});
        }
        {
            var Q0;
            Q0=qCreatedBy(id+"F29.planeOp",FACE);
            var sketch = newSketch(context, id + "F32", { "sketchPlane" : qUnion([Q0])});
            skCircle(sketch, "E72", {"center": v(-0.05, 25) * mm, "radius": 5 * mm});
            skSolve(sketch);
        }
        {
            var Q0;
            Q0 = qSketchRegion(id + "F32", true);
            var Q1;
            Q1=makeQuery(id+"F21.boolean.opBoolean","SPLIT",FACE,{"disambiguationData":[TD([makeQuery(id+"F1.opExtrude","CAP_FACE",FACE,{"disambiguationData":[OSD([sQuery(id+"F0.wireOp",EDGE,"E0.bottom"),sQuery(id+"F0.wireOp",EDGE,"E0.top"),sQuery(id+"F0.wireOp",EDGE,"E0.left"),sQuery(id+"F0.wireOp",EDGE,"E0.right")])],"isStart":false})])],"derivedFrom":makeQuery(id+"F7.boolean.opBoolean","COPY",FACE,{"derivedFrom":makeQuery(id+"F7.opExtrude","SWEPT_FACE",FACE,{"disambiguationData":[OSD([sQuery(id+"F6.wireOp",EDGE,"E22")])]})})});
            extrude(context, id + "F33", {"entities" : qUnion([Q0]), "operationType" : NewBodyOperationType.REMOVE, "endBound" : BoundingType.UP_TO_SURFACE, "depth" : 25 * mm, "endBoundEntityFace" : qUnion([Q1]), "offsetDistance" : 25 * mm});
        }
        {
            var Q0;
            Q0=sQuery(id+"F9.wireOp",VERTEX,"E27.endSnap0");
            var Q1;
            {var subQ0=sQuery(id+"F24.wireOp",EDGE,"E69");var subQ1=sQuery(id+"F24.wireOp",EDGE,"E68");Q1=makeQuery(id+"F25.boolean.opBoolean","COPY",VERTEX,{"disambiguationData":[TD([makeQuery(id+"F25.opExtrude","CAP_FACE",FACE,{"disambiguationData":[OSD([sQuery(id+"F24.wireOp",EDGE,"E65"),sQuery(id+"F24.wireOp",EDGE,"E66"),sQuery(id+"F24.wireOp",EDGE,"E67"),subQ1,subQ0,sQuery(id+"F24.wireOp",EDGE,"E70")])],"isStart":true})])],"derivedFrom":makeQuery(id+"F25.opExtrude","CAP_VERTEX",VERTEX,{"disambiguationData":[OSD([subQ1,subQ0])],"isStart":true})});}
            var Q2;
            {var subQ1=sQuery(id+"F24.wireOp",EDGE,"E70");var subQ2=sQuery(id+"F24.wireOp",EDGE,"E69");Q2=makeQuery(id+"F25.boolean.opBoolean","COPY",VERTEX,{"disambiguationData":[TD([makeQuery(id+"F25.opExtrude","CAP_FACE",FACE,{"disambiguationData":[OSD([sQuery(id+"F24.wireOp",EDGE,"E65"),sQuery(id+"F24.wireOp",EDGE,"E66"),sQuery(id+"F24.wireOp",EDGE,"E67"),sQuery(id+"F24.wireOp",EDGE,"E68"),subQ2,subQ1])],"isStart":true})])],"derivedFrom":makeQuery(id+"F25.opExtrude","CAP_VERTEX",VERTEX,{"disambiguationData":[OSD([subQ2,subQ1])],"isStart":true})});}
            cPlane(context, id + "F34", {"entities" : qUnion([Q0, Q1, Q2]), "cplaneType" : CPlaneType.THREE_POINT, "offset" : 25 * mm, "width" : 150 * mm, "height" : 150 * mm});
        }
        {
            var Q0;
            Q0=qCreatedBy(id+"F34.planeOp",FACE);
            var sketch = newSketch(context, id + "F35", { "sketchPlane" : qUnion([Q0])});
            skCircle(sketch, "E73", {"center": v(-24.98, 0) * mm, "radius": 2.55 * mm});
            skSolve(sketch);
        }
        {
            var Q0;
            Q0 = qSketchRegion(id + "F35", true);
            var Q1;
            Q1=makeQuery(id+"F1.opExtrude","CAP_VERTEX",VERTEX,{"disambiguationData":[OSD([sQuery(id+"F0.wireOp",EDGE,"E0.bottom"),sQuery(id+"F0.wireOp",EDGE,"E0.right")])],"isStart":true});
            extrude(context, id + "F36", {"entities" : qUnion([Q0]), "operationType" : NewBodyOperationType.REMOVE, "endBound" : BoundingType.UP_TO_VERTEX, "oppositeDirection" : true, "depth" : 25 * mm, "endBoundEntityVertex" : qUnion([Q1]), "offsetDistance" : 25 * mm});
        }
        {
            var Q0;
            Q0=qCreatedBy(id+"F34.planeOp",FACE);
            var sketch = newSketch(context, id + "F37", { "sketchPlane" : qUnion([Q0])});
            skCircle(sketch, "E74", {"center": v(-24.98, 0) * mm, "radius": 5 * mm});
            skSolve(sketch);
        }
        {
            var Q0;
            Q0 = qSketchRegion(id + "F37", true);
            extrude(context, id + "F38", {"entities" : qUnion([Q0]), "operationType" : NewBodyOperationType.REMOVE, "depth" : 25 * mm, "offsetDistance" : 25 * mm});
        }
        {
            var Q0;
            Q0=sQuery(id+"F16.wireOp",VERTEX,"E63");
            var Q1;
            {var subQ1=sQuery(id+"F24.wireOp",EDGE,"E70");var subQ2=sQuery(id+"F24.wireOp",EDGE,"E65");Q1=makeQuery(id+"F25.boolean.opBoolean","COPY",VERTEX,{"disambiguationData":[TD([makeQuery(id+"F25.opExtrude","CAP_FACE",FACE,{"disambiguationData":[OSD([subQ2,sQuery(id+"F24.wireOp",EDGE,"E66"),sQuery(id+"F24.wireOp",EDGE,"E67"),sQuery(id+"F24.wireOp",EDGE,"E68"),sQuery(id+"F24.wireOp",EDGE,"E69"),subQ1])],"isStart":true})])],"derivedFrom":makeQuery(id+"F25.opExtrude","CAP_VERTEX",VERTEX,{"disambiguationData":[OSD([subQ2,subQ1])],"isStart":true})});}
            var Q2;
            {var subQ0=sQuery(id+"F24.wireOp",EDGE,"E66");var subQ1=sQuery(id+"F24.wireOp",EDGE,"E65");Q2=makeQuery(id+"F25.boolean.opBoolean","COPY",VERTEX,{"disambiguationData":[TD([makeQuery(id+"F25.opExtrude","CAP_FACE",FACE,{"disambiguationData":[OSD([subQ1,subQ0,sQuery(id+"F24.wireOp",EDGE,"E67"),sQuery(id+"F24.wireOp",EDGE,"E68"),sQuery(id+"F24.wireOp",EDGE,"E69"),sQuery(id+"F24.wireOp",EDGE,"E70")])],"isStart":true})])],"derivedFrom":makeQuery(id+"F25.opExtrude","CAP_VERTEX",VERTEX,{"disambiguationData":[OSD([subQ1,subQ0])],"isStart":true})});}
            cPlane(context, id + "F39", {"entities" : qUnion([Q0, Q1, Q2]), "cplaneType" : CPlaneType.THREE_POINT, "offset" : 25 * mm, "width" : 150 * mm, "height" : 150 * mm});
        }
        {
            var Q0;
            Q0=qCreatedBy(id+"F39.planeOp",FACE);
            var sketch = newSketch(context, id + "F40", { "sketchPlane" : qUnion([Q0])});
            skCircle(sketch, "E75", {"center": v(0, 25) * mm, "radius": 2.55 * mm});
            skSolve(sketch);
        }
        {
            var Q0;
            Q0 = qSketchRegion(id + "F40", true);
            var Q1;
            Q1=makeQuery(id+"F1.opExtrude","CAP_VERTEX",VERTEX,{"disambiguationData":[OSD([sQuery(id+"F0.wireOp",EDGE,"E0.top"),sQuery(id+"F0.wireOp",EDGE,"E0.left")])],"isStart":true});
            extrude(context, id + "F41", {"entities" : qUnion([Q0]), "operationType" : NewBodyOperationType.REMOVE, "endBound" : BoundingType.UP_TO_VERTEX, "oppositeDirection" : true, "depth" : 25 * mm, "endBoundEntityVertex" : qUnion([Q1]), "offsetDistance" : 25 * mm});
        }
        {
            var Q0;
            Q0=qCreatedBy(id+"F39.planeOp",FACE);
            var sketch = newSketch(context, id + "F42", { "sketchPlane" : qUnion([Q0])});
            skCircle(sketch, "E76", {"center": v(0, 25) * mm, "radius": 5 * mm});
            skSolve(sketch);
        }
        {
            var Q0;
            Q0 = qSketchRegion(id + "F42", true);
            extrude(context, id + "F43", {"entities" : qUnion([Q0]), "operationType" : NewBodyOperationType.REMOVE, "depth" : 7.4 * mm, "offsetDistance" : 25 * mm});
        }
        {
            var Q0;
            {var subQ0=makeQuery(id+"F7.boolean.opBoolean","COPY",FACE,{"derivedFrom":makeQuery(id+"F7.opExtrude","SWEPT_FACE",FACE,{"disambiguationData":[OSD([sQuery(id+"F6.wireOp",EDGE,"E22")])]})});var subQ1=sQuery(id+"F0.wireOp",EDGE,"E0.top");var subQ3=makeQuery(id+"F21.opExtrude","SWEPT_FACE",FACE,{"disambiguationData":[OSD([sQuery(id+"F20.wireOp",EDGE,"E64")])]});var subQ4=makeQuery(id+"F25.opExtrude","CAP_FACE",FACE,{"disambiguationData":[OSD([sQuery(id+"F24.wireOp",EDGE,"E65"),sQuery(id+"F24.wireOp",EDGE,"E66"),sQuery(id+"F24.wireOp",EDGE,"E67"),sQuery(id+"F24.wireOp",EDGE,"E68"),sQuery(id+"F24.wireOp",EDGE,"E69"),sQuery(id+"F24.wireOp",EDGE,"E70")])],"isStart":true});Q0=makeQuery(id+"F33.boolean.opBoolean","SPLIT",EDGE,{"disambiguationData":[TD([makeQuery(id+"F21.boolean.opBoolean","COPY",FACE,{"disambiguationData":[TD([makeQuery(id+"F1.opExtrude","SWEPT_FACE",FACE,{"disambiguationData":[OSD([subQ1])]})])],"derivedFrom":subQ3})])],"derivedFrom":makeQuery(id+"F25.boolean.opBoolean","INTERSECT",EDGE,{"derivedFrom":[makeQuery(id+"F21.boolean.opBoolean","SPLIT",FACE,{"disambiguationData":[TD([makeQuery(id+"F1.opExtrude","CAP_FACE",FACE,{"disambiguationData":[OSD([sQuery(id+"F0.wireOp",EDGE,"E0.bottom"),subQ1,sQuery(id+"F0.wireOp",EDGE,"E0.left"),sQuery(id+"F0.wireOp",EDGE,"E0.right")])],"isStart":false})])],"derivedFrom":subQ0}),subQ4]})});}
            var Q1;
            {var subQ0=makeQuery(id+"F7.boolean.opBoolean","COPY",FACE,{"derivedFrom":makeQuery(id+"F7.opExtrude","SWEPT_FACE",FACE,{"disambiguationData":[OSD([sQuery(id+"F6.wireOp",EDGE,"E22")])]})});var subQ1=makeQuery(id+"F21.boolean.opBoolean","COPY",FACE,{"disambiguationData":[TD([makeQuery(id+"F1.opExtrude","SWEPT_FACE",FACE,{"disambiguationData":[OSD([sQuery(id+"F0.wireOp",EDGE,"E0.top")])]})])],"derivedFrom":makeQuery(id+"F21.opExtrude","SWEPT_FACE",FACE,{"disambiguationData":[OSD([sQuery(id+"F20.wireOp",EDGE,"E64")])]})});var subQ2=makeQuery(id+"F25.opExtrude","CAP_FACE",FACE,{"disambiguationData":[OSD([sQuery(id+"F24.wireOp",EDGE,"E65"),sQuery(id+"F24.wireOp",EDGE,"E66"),sQuery(id+"F24.wireOp",EDGE,"E67"),sQuery(id+"F24.wireOp",EDGE,"E68"),sQuery(id+"F24.wireOp",EDGE,"E69"),sQuery(id+"F24.wireOp",EDGE,"E70")])],"isStart":true});Q1=makeQuery(id+"F43.boolean.opBoolean","SPLIT",EDGE,{"disambiguationData":[TD([subQ0])],"derivedFrom":makeQuery(id+"F25.boolean.opBoolean","INTERSECT",EDGE,{"derivedFrom":[subQ1,subQ2]})});}
            var Q2;
            {var subQ0=makeQuery(id+"F14.boolean.opBoolean","COPY",FACE,{"derivedFrom":makeQuery(id+"F14.opExtrude","SWEPT_FACE",FACE,{"disambiguationData":[OSD([sQuery(id+"F13.wireOp",EDGE,"E44")])]})});var subQ1=makeQuery(id+"F21.boolean.opBoolean","COPY",FACE,{"disambiguationData":[TD([makeQuery(id+"F1.opExtrude","SWEPT_FACE",FACE,{"disambiguationData":[OSD([sQuery(id+"F0.wireOp",EDGE,"E0.top")])]})])],"derivedFrom":makeQuery(id+"F21.opExtrude","SWEPT_FACE",FACE,{"disambiguationData":[OSD([sQuery(id+"F20.wireOp",EDGE,"E64")])]})});var subQ2=makeQuery(id+"F25.opExtrude","CAP_FACE",FACE,{"disambiguationData":[OSD([sQuery(id+"F24.wireOp",EDGE,"E65"),sQuery(id+"F24.wireOp",EDGE,"E66"),sQuery(id+"F24.wireOp",EDGE,"E67"),sQuery(id+"F24.wireOp",EDGE,"E68"),sQuery(id+"F24.wireOp",EDGE,"E69"),sQuery(id+"F24.wireOp",EDGE,"E70")])],"isStart":true});Q2=makeQuery(id+"F43.boolean.opBoolean","SPLIT",EDGE,{"disambiguationData":[TD([subQ0])],"derivedFrom":makeQuery(id+"F25.boolean.opBoolean","INTERSECT",EDGE,{"derivedFrom":[subQ1,subQ2]})});}
            var Q3;
            {var subQ0=makeQuery(id+"F14.boolean.opBoolean","COPY",FACE,{"derivedFrom":makeQuery(id+"F14.opExtrude","SWEPT_FACE",FACE,{"disambiguationData":[OSD([sQuery(id+"F13.wireOp",EDGE,"E44")])]})});var subQ2=makeQuery(id+"F21.opExtrude","SWEPT_FACE",FACE,{"disambiguationData":[OSD([sQuery(id+"F20.wireOp",EDGE,"E64")])]});var subQ3=makeQuery(id+"F25.opExtrude","CAP_FACE",FACE,{"disambiguationData":[OSD([sQuery(id+"F24.wireOp",EDGE,"E65"),sQuery(id+"F24.wireOp",EDGE,"E66"),sQuery(id+"F24.wireOp",EDGE,"E67"),sQuery(id+"F24.wireOp",EDGE,"E68"),sQuery(id+"F24.wireOp",EDGE,"E69"),sQuery(id+"F24.wireOp",EDGE,"E70")])],"isStart":true});Q3=makeQuery(id+"F38.boolean.opBoolean","SPLIT",EDGE,{"disambiguationData":[TD([makeQuery(id+"F21.boolean.opBoolean","COPY",FACE,{"disambiguationData":[TD([makeQuery(id+"F1.opExtrude","SWEPT_FACE",FACE,{"disambiguationData":[OSD([sQuery(id+"F0.wireOp",EDGE,"E0.top")])]})])],"derivedFrom":subQ2})])],"derivedFrom":makeQuery(id+"F25.boolean.opBoolean","INTERSECT",EDGE,{"derivedFrom":[makeQuery(id+"F21.boolean.opBoolean","SPLIT",FACE,{"disambiguationData":[TD([makeQuery(id+"F1.opExtrude","SWEPT_FACE",FACE,{"disambiguationData":[OSD([sQuery(id+"F0.wireOp",EDGE,"E0.right")])]})])],"derivedFrom":subQ0}),subQ3]})});}
            var Q4;
            {var subQ0=makeQuery(id+"F7.boolean.opBoolean","COPY",FACE,{"derivedFrom":makeQuery(id+"F7.opExtrude","SWEPT_FACE",FACE,{"disambiguationData":[OSD([sQuery(id+"F6.wireOp",EDGE,"E22")])]})});var subQ1=makeQuery(id+"F14.boolean.opBoolean","COPY",FACE,{"derivedFrom":makeQuery(id+"F14.opExtrude","SWEPT_FACE",FACE,{"disambiguationData":[OSD([sQuery(id+"F13.wireOp",EDGE,"E44")])]})});var subQ2=makeQuery(id+"F25.opExtrude","CAP_FACE",FACE,{"disambiguationData":[OSD([sQuery(id+"F24.wireOp",EDGE,"E65"),sQuery(id+"F24.wireOp",EDGE,"E66"),sQuery(id+"F24.wireOp",EDGE,"E67"),sQuery(id+"F24.wireOp",EDGE,"E68"),sQuery(id+"F24.wireOp",EDGE,"E69"),sQuery(id+"F24.wireOp",EDGE,"E70")])],"isStart":true});Q4=makeQuery(id+"F38.boolean.opBoolean","SPLIT",EDGE,{"disambiguationData":[TD([subQ0])],"derivedFrom":makeQuery(id+"F25.boolean.opBoolean","INTERSECT",EDGE,{"derivedFrom":[makeQuery(id+"F21.boolean.opBoolean","SPLIT",FACE,{"disambiguationData":[TD([makeQuery(id+"F1.opExtrude","SWEPT_FACE",FACE,{"disambiguationData":[OSD([sQuery(id+"F0.wireOp",EDGE,"E0.right")])]})])],"derivedFrom":subQ1}),subQ2]})});}
            var Q5;
            {var subQ0=makeQuery(id+"F7.boolean.opBoolean","COPY",FACE,{"derivedFrom":makeQuery(id+"F7.opExtrude","SWEPT_FACE",FACE,{"disambiguationData":[OSD([sQuery(id+"F6.wireOp",EDGE,"E22")])]})});var subQ1=makeQuery(id+"F14.boolean.opBoolean","COPY",FACE,{"derivedFrom":makeQuery(id+"F14.opExtrude","SWEPT_FACE",FACE,{"disambiguationData":[OSD([sQuery(id+"F13.wireOp",EDGE,"E44")])]})});var subQ2=makeQuery(id+"F25.opExtrude","CAP_FACE",FACE,{"disambiguationData":[OSD([sQuery(id+"F24.wireOp",EDGE,"E65"),sQuery(id+"F24.wireOp",EDGE,"E66"),sQuery(id+"F24.wireOp",EDGE,"E67"),sQuery(id+"F24.wireOp",EDGE,"E68"),sQuery(id+"F24.wireOp",EDGE,"E69"),sQuery(id+"F24.wireOp",EDGE,"E70")])],"isStart":true});Q5=makeQuery(id+"F33.boolean.opBoolean","SPLIT",EDGE,{"disambiguationData":[TD([subQ1])],"derivedFrom":makeQuery(id+"F25.boolean.opBoolean","INTERSECT",EDGE,{"derivedFrom":[makeQuery(id+"F21.boolean.opBoolean","SPLIT",FACE,{"disambiguationData":[TD([makeQuery(id+"F1.opExtrude","CAP_FACE",FACE,{"disambiguationData":[OSD([sQuery(id+"F0.wireOp",EDGE,"E0.bottom"),sQuery(id+"F0.wireOp",EDGE,"E0.top"),sQuery(id+"F0.wireOp",EDGE,"E0.left"),sQuery(id+"F0.wireOp",EDGE,"E0.right")])],"isStart":false})])],"derivedFrom":subQ0}),subQ2]})});}
            fillet(context, id + "F44", {"entities" : qUnion([Q0, Q1, Q2, Q3, Q4, Q5]), "radius" : 10 * mm, "tangentPropagation" : true});
        }
        {
            var Q0;
            {var subQ0=makeQuery(id+"F7.boolean.opBoolean","COPY",FACE,{"derivedFrom":makeQuery(id+"F7.opExtrude","SWEPT_FACE",FACE,{"disambiguationData":[OSD([sQuery(id+"F6.wireOp",EDGE,"E22")])]})});var subQ1=sQuery(id+"F13.wireOp",EDGE,"E44");var subQ2=makeQuery(id+"F21.opExtrude","SWEPT_FACE",FACE,{"disambiguationData":[OSD([sQuery(id+"F20.wireOp",EDGE,"E64")])]});var subQ3=makeQuery(id+"F14.boolean.opBoolean","COPY",FACE,{"derivedFrom":makeQuery(id+"F14.opExtrude","SWEPT_FACE",FACE,{"disambiguationData":[OSD([subQ1])]})});var subQ4=sQuery(id+"F0.wireOp",EDGE,"E0.top");var subQ5=makeQuery(id+"F25.opExtrude","CAP_FACE",FACE,{"disambiguationData":[OSD([sQuery(id+"F24.wireOp",EDGE,"E65"),sQuery(id+"F24.wireOp",EDGE,"E66"),sQuery(id+"F24.wireOp",EDGE,"E67"),sQuery(id+"F24.wireOp",EDGE,"E68"),sQuery(id+"F24.wireOp",EDGE,"E69"),sQuery(id+"F24.wireOp",EDGE,"E70")])],"isStart":true});Q0=makeQuery(id+"F44.opFillet","BLEND_EDGE",EDGE,{"blendedFrom":[makeQuery(id+"F33.boolean.opBoolean","SPLIT",EDGE,{"disambiguationData":[TD([makeQuery(id+"F21.boolean.opBoolean","COPY",FACE,{"disambiguationData":[TD([makeQuery(id+"F1.opExtrude","SWEPT_FACE",FACE,{"disambiguationData":[OSD([subQ4])]})])],"derivedFrom":subQ2})])],"derivedFrom":makeQuery(id+"F25.boolean.opBoolean","INTERSECT",EDGE,{"derivedFrom":[makeQuery(id+"F21.boolean.opBoolean","SPLIT",FACE,{"disambiguationData":[TD([makeQuery(id+"F1.opExtrude","CAP_FACE",FACE,{"disambiguationData":[OSD([sQuery(id+"F0.wireOp",EDGE,"E0.bottom"),subQ4,sQuery(id+"F0.wireOp",EDGE,"E0.left"),sQuery(id+"F0.wireOp",EDGE,"E0.right")])],"isStart":false})])],"derivedFrom":subQ0}),subQ5]})}),makeQuery(id+"F21.boolean.opBoolean","SPLIT",FACE,{"disambiguationData":[TD([makeQuery(id+"F15.boolean.opBoolean","COPY",FACE,{"derivedFrom":makeQuery(id+"F15.opLoft","SWEPT_FACE",FACE,{"disambiguationData":[OSD([sQuery(id+"F9.wireOp",EDGE,"E26"),subQ1])]})})])],"derivedFrom":subQ3})],"blendedInto":[makeQuery(id+"F21.boolean.opBoolean","SPLIT",FACE,{"disambiguationData":[TD([makeQuery(id+"F15.boolean.opBoolean","COPY",FACE,{"derivedFrom":makeQuery(id+"F15.opLoft","SWEPT_FACE",FACE,{"disambiguationData":[OSD([sQuery(id+"F9.wireOp",EDGE,"E26"),subQ1])]})})])],"derivedFrom":subQ3})]});}
            var Q1;
            Q1=makeQuery(id+"F21.boolean.opBoolean","SPLIT",EDGE,{"disambiguationData":[OD(2.0)],"derivedFrom":makeQuery(id+"F14.boolean.opBoolean","INTERSECT",EDGE,{"derivedFrom":[makeQuery(id+"F7.boolean.opBoolean","COPY",FACE,{"derivedFrom":makeQuery(id+"F7.opExtrude","SWEPT_FACE",FACE,{"disambiguationData":[OSD([sQuery(id+"F6.wireOp",EDGE,"E22")])]})}),makeQuery(id+"F14.opExtrude","SWEPT_FACE",FACE,{"disambiguationData":[OSD([sQuery(id+"F13.wireOp",EDGE,"E44")])]})]})});
            var Q2;
            {var subQ0=makeQuery(id+"F7.boolean.opBoolean","COPY",FACE,{"derivedFrom":makeQuery(id+"F7.opExtrude","SWEPT_FACE",FACE,{"disambiguationData":[OSD([sQuery(id+"F6.wireOp",EDGE,"E22")])]})});var subQ1=sQuery(id+"F13.wireOp",EDGE,"E44");var subQ2=makeQuery(id+"F21.opExtrude","SWEPT_FACE",FACE,{"disambiguationData":[OSD([sQuery(id+"F20.wireOp",EDGE,"E64")])]});var subQ3=makeQuery(id+"F14.boolean.opBoolean","COPY",FACE,{"derivedFrom":makeQuery(id+"F14.opExtrude","SWEPT_FACE",FACE,{"disambiguationData":[OSD([subQ1])]})});var subQ4=makeQuery(id+"F21.boolean.opBoolean","COPY",FACE,{"disambiguationData":[TD([makeQuery(id+"F1.opExtrude","SWEPT_FACE",FACE,{"disambiguationData":[OSD([sQuery(id+"F0.wireOp",EDGE,"E0.top")])]})])],"derivedFrom":subQ2});var subQ5=makeQuery(id+"F25.opExtrude","CAP_FACE",FACE,{"disambiguationData":[OSD([sQuery(id+"F24.wireOp",EDGE,"E65"),sQuery(id+"F24.wireOp",EDGE,"E66"),sQuery(id+"F24.wireOp",EDGE,"E67"),sQuery(id+"F24.wireOp",EDGE,"E68"),sQuery(id+"F24.wireOp",EDGE,"E69"),sQuery(id+"F24.wireOp",EDGE,"E70")])],"isStart":true});Q2=makeQuery(id+"F44.opFillet","BLEND_EDGE",EDGE,{"blendedFrom":[makeQuery(id+"F43.boolean.opBoolean","SPLIT",EDGE,{"disambiguationData":[TD([subQ0])],"derivedFrom":makeQuery(id+"F25.boolean.opBoolean","INTERSECT",EDGE,{"derivedFrom":[subQ4,subQ5]})}),makeQuery(id+"F21.boolean.opBoolean","SPLIT",FACE,{"disambiguationData":[TD([makeQuery(id+"F15.boolean.opBoolean","COPY",FACE,{"derivedFrom":makeQuery(id+"F15.opLoft","SWEPT_FACE",FACE,{"disambiguationData":[OSD([sQuery(id+"F9.wireOp",EDGE,"E26"),subQ1])]})})])],"derivedFrom":subQ3})],"blendedInto":[makeQuery(id+"F21.boolean.opBoolean","SPLIT",FACE,{"disambiguationData":[TD([makeQuery(id+"F15.boolean.opBoolean","COPY",FACE,{"derivedFrom":makeQuery(id+"F15.opLoft","SWEPT_FACE",FACE,{"disambiguationData":[OSD([sQuery(id+"F9.wireOp",EDGE,"E26"),subQ1])]})})])],"derivedFrom":subQ3})]});}
            var Q3;
            Q3=makeQuery(id+"F21.boolean.opBoolean","INTERSECT",EDGE,{"disambiguationData":[OD(3.0)],"derivedFrom":[makeQuery(id+"F14.boolean.opBoolean","COPY",FACE,{"derivedFrom":makeQuery(id+"F14.opExtrude","SWEPT_FACE",FACE,{"disambiguationData":[OSD([sQuery(id+"F13.wireOp",EDGE,"E44")])]})}),makeQuery(id+"F21.opExtrude","SWEPT_FACE",FACE,{"disambiguationData":[OSD([sQuery(id+"F20.wireOp",EDGE,"E64")])]})]});
            var Q4;
            Q4=makeQuery(id+"F21.boolean.opBoolean","INTERSECT",EDGE,{"disambiguationData":[OD(3.0)],"derivedFrom":[makeQuery(id+"F7.boolean.opBoolean","COPY",FACE,{"derivedFrom":makeQuery(id+"F7.opExtrude","SWEPT_FACE",FACE,{"disambiguationData":[OSD([sQuery(id+"F6.wireOp",EDGE,"E22")])]})}),makeQuery(id+"F21.opExtrude","SWEPT_FACE",FACE,{"disambiguationData":[OSD([sQuery(id+"F20.wireOp",EDGE,"E64")])]})]});
            var Q5;
            {var subQ0=sQuery(id+"F6.wireOp",EDGE,"E22");var subQ1=makeQuery(id+"F14.boolean.opBoolean","COPY",FACE,{"derivedFrom":makeQuery(id+"F14.opExtrude","SWEPT_FACE",FACE,{"disambiguationData":[OSD([sQuery(id+"F13.wireOp",EDGE,"E44")])]})});var subQ2=makeQuery(id+"F21.opExtrude","SWEPT_FACE",FACE,{"disambiguationData":[OSD([sQuery(id+"F20.wireOp",EDGE,"E64")])]});var subQ3=makeQuery(id+"F7.boolean.opBoolean","COPY",FACE,{"derivedFrom":makeQuery(id+"F7.opExtrude","SWEPT_FACE",FACE,{"disambiguationData":[OSD([subQ0])]})});var subQ4=makeQuery(id+"F21.boolean.opBoolean","COPY",FACE,{"disambiguationData":[TD([makeQuery(id+"F1.opExtrude","SWEPT_FACE",FACE,{"disambiguationData":[OSD([sQuery(id+"F0.wireOp",EDGE,"E0.top")])]})])],"derivedFrom":subQ2});var subQ5=makeQuery(id+"F25.opExtrude","CAP_FACE",FACE,{"disambiguationData":[OSD([sQuery(id+"F24.wireOp",EDGE,"E65"),sQuery(id+"F24.wireOp",EDGE,"E66"),sQuery(id+"F24.wireOp",EDGE,"E67"),sQuery(id+"F24.wireOp",EDGE,"E68"),sQuery(id+"F24.wireOp",EDGE,"E69"),sQuery(id+"F24.wireOp",EDGE,"E70")])],"isStart":true});Q5=makeQuery(id+"F44.opFillet","BLEND_EDGE",EDGE,{"blendedFrom":[makeQuery(id+"F43.boolean.opBoolean","SPLIT",EDGE,{"disambiguationData":[TD([subQ1])],"derivedFrom":makeQuery(id+"F25.boolean.opBoolean","INTERSECT",EDGE,{"derivedFrom":[subQ4,subQ5]})}),makeQuery(id+"F21.boolean.opBoolean","SPLIT",FACE,{"disambiguationData":[TD([makeQuery(id+"F8.boolean.opBoolean","COPY",FACE,{"derivedFrom":makeQuery(id+"F8.opLoft","SWEPT_FACE",FACE,{"disambiguationData":[OSD([sQuery(id+"F2.wireOp",EDGE,"E18"),subQ0])]})})])],"derivedFrom":subQ3})],"blendedInto":[makeQuery(id+"F21.boolean.opBoolean","SPLIT",FACE,{"disambiguationData":[TD([makeQuery(id+"F8.boolean.opBoolean","COPY",FACE,{"derivedFrom":makeQuery(id+"F8.opLoft","SWEPT_FACE",FACE,{"disambiguationData":[OSD([sQuery(id+"F2.wireOp",EDGE,"E18"),subQ0])]})})])],"derivedFrom":subQ3})]});}
            var Q6;
            {var subQ0=sQuery(id+"F6.wireOp",EDGE,"E22");var subQ1=makeQuery(id+"F14.boolean.opBoolean","COPY",FACE,{"derivedFrom":makeQuery(id+"F14.opExtrude","SWEPT_FACE",FACE,{"disambiguationData":[OSD([sQuery(id+"F13.wireOp",EDGE,"E44")])]})});var subQ2=makeQuery(id+"F21.opExtrude","SWEPT_FACE",FACE,{"disambiguationData":[OSD([sQuery(id+"F20.wireOp",EDGE,"E64")])]});var subQ3=makeQuery(id+"F7.boolean.opBoolean","COPY",FACE,{"derivedFrom":makeQuery(id+"F7.opExtrude","SWEPT_FACE",FACE,{"disambiguationData":[OSD([subQ0])]})});var subQ4=makeQuery(id+"F25.opExtrude","CAP_FACE",FACE,{"disambiguationData":[OSD([sQuery(id+"F24.wireOp",EDGE,"E65"),sQuery(id+"F24.wireOp",EDGE,"E66"),sQuery(id+"F24.wireOp",EDGE,"E67"),sQuery(id+"F24.wireOp",EDGE,"E68"),sQuery(id+"F24.wireOp",EDGE,"E69"),sQuery(id+"F24.wireOp",EDGE,"E70")])],"isStart":true});Q6=makeQuery(id+"F44.opFillet","BLEND_EDGE",EDGE,{"blendedFrom":[makeQuery(id+"F38.boolean.opBoolean","SPLIT",EDGE,{"disambiguationData":[TD([makeQuery(id+"F21.boolean.opBoolean","COPY",FACE,{"disambiguationData":[TD([makeQuery(id+"F1.opExtrude","SWEPT_FACE",FACE,{"disambiguationData":[OSD([sQuery(id+"F0.wireOp",EDGE,"E0.top")])]})])],"derivedFrom":subQ2})])],"derivedFrom":makeQuery(id+"F25.boolean.opBoolean","INTERSECT",EDGE,{"derivedFrom":[makeQuery(id+"F21.boolean.opBoolean","SPLIT",FACE,{"disambiguationData":[TD([makeQuery(id+"F1.opExtrude","SWEPT_FACE",FACE,{"disambiguationData":[OSD([sQuery(id+"F0.wireOp",EDGE,"E0.right")])]})])],"derivedFrom":subQ1}),subQ4]})}),makeQuery(id+"F21.boolean.opBoolean","SPLIT",FACE,{"disambiguationData":[TD([makeQuery(id+"F8.boolean.opBoolean","COPY",FACE,{"derivedFrom":makeQuery(id+"F8.opLoft","SWEPT_FACE",FACE,{"disambiguationData":[OSD([sQuery(id+"F2.wireOp",EDGE,"E18"),subQ0])]})})])],"derivedFrom":subQ3})],"blendedInto":[makeQuery(id+"F21.boolean.opBoolean","SPLIT",FACE,{"disambiguationData":[TD([makeQuery(id+"F8.boolean.opBoolean","COPY",FACE,{"derivedFrom":makeQuery(id+"F8.opLoft","SWEPT_FACE",FACE,{"disambiguationData":[OSD([sQuery(id+"F2.wireOp",EDGE,"E18"),subQ0])]})})])],"derivedFrom":subQ3})]});}
            var Q7;
            Q7=makeQuery(id+"F21.boolean.opBoolean","SPLIT",EDGE,{"disambiguationData":[OD(1.0)],"derivedFrom":makeQuery(id+"F14.boolean.opBoolean","INTERSECT",EDGE,{"derivedFrom":[makeQuery(id+"F7.boolean.opBoolean","COPY",FACE,{"derivedFrom":makeQuery(id+"F7.opExtrude","SWEPT_FACE",FACE,{"disambiguationData":[OSD([sQuery(id+"F6.wireOp",EDGE,"E22")])]})}),makeQuery(id+"F14.opExtrude","SWEPT_FACE",FACE,{"disambiguationData":[OSD([sQuery(id+"F13.wireOp",EDGE,"E44")])]})]})});
            var Q8;
            Q8=makeQuery(id+"F21.boolean.opBoolean","INTERSECT",EDGE,{"disambiguationData":[OD(0.0)],"derivedFrom":[makeQuery(id+"F7.boolean.opBoolean","COPY",FACE,{"derivedFrom":makeQuery(id+"F7.opExtrude","SWEPT_FACE",FACE,{"disambiguationData":[OSD([sQuery(id+"F6.wireOp",EDGE,"E22")])]})}),makeQuery(id+"F21.opExtrude","SWEPT_FACE",FACE,{"disambiguationData":[OSD([sQuery(id+"F20.wireOp",EDGE,"E64")])]})]});
            var Q9;
            {var subQ0=makeQuery(id+"F7.boolean.opBoolean","COPY",FACE,{"derivedFrom":makeQuery(id+"F7.opExtrude","SWEPT_FACE",FACE,{"disambiguationData":[OSD([sQuery(id+"F6.wireOp",EDGE,"E22")])]})});var subQ1=makeQuery(id+"F14.boolean.opBoolean","COPY",FACE,{"derivedFrom":makeQuery(id+"F14.opExtrude","SWEPT_FACE",FACE,{"disambiguationData":[OSD([sQuery(id+"F13.wireOp",EDGE,"E44")])]})});var subQ2=sQuery(id+"F20.wireOp",EDGE,"E64");var subQ3=makeQuery(id+"F21.opExtrude","SWEPT_FACE",FACE,{"disambiguationData":[OSD([subQ2])]});var subQ4=makeQuery(id+"F25.opExtrude","CAP_FACE",FACE,{"disambiguationData":[OSD([sQuery(id+"F24.wireOp",EDGE,"E65"),sQuery(id+"F24.wireOp",EDGE,"E66"),sQuery(id+"F24.wireOp",EDGE,"E67"),sQuery(id+"F24.wireOp",EDGE,"E68"),sQuery(id+"F24.wireOp",EDGE,"E69"),sQuery(id+"F24.wireOp",EDGE,"E70")])],"isStart":true});Q9=makeQuery(id+"F44.opFillet","BLEND_EDGE",EDGE,{"blendedFrom":[makeQuery(id+"F33.boolean.opBoolean","SPLIT",EDGE,{"disambiguationData":[TD([subQ1])],"derivedFrom":makeQuery(id+"F25.boolean.opBoolean","INTERSECT",EDGE,{"derivedFrom":[makeQuery(id+"F21.boolean.opBoolean","SPLIT",FACE,{"disambiguationData":[TD([makeQuery(id+"F1.opExtrude","CAP_FACE",FACE,{"disambiguationData":[OSD([sQuery(id+"F0.wireOp",EDGE,"E0.bottom"),sQuery(id+"F0.wireOp",EDGE,"E0.top"),sQuery(id+"F0.wireOp",EDGE,"E0.left"),sQuery(id+"F0.wireOp",EDGE,"E0.right")])],"isStart":false})])],"derivedFrom":subQ0}),subQ4]})}),makeQuery(id+"F21.boolean.opBoolean","COPY",FACE,{"disambiguationData":[TD([makeQuery(id+"F21.opExtrude","CAP_FACE",FACE,{"disambiguationData":[OSD([subQ2])],"isStart":true})])],"derivedFrom":subQ3})],"blendedInto":[makeQuery(id+"F21.boolean.opBoolean","COPY",FACE,{"disambiguationData":[TD([makeQuery(id+"F21.opExtrude","CAP_FACE",FACE,{"disambiguationData":[OSD([subQ2])],"isStart":true})])],"derivedFrom":subQ3})]});}
            var Q10;
            {var subQ0=makeQuery(id+"F7.boolean.opBoolean","COPY",FACE,{"derivedFrom":makeQuery(id+"F7.opExtrude","SWEPT_FACE",FACE,{"disambiguationData":[OSD([sQuery(id+"F6.wireOp",EDGE,"E22")])]})});var subQ1=makeQuery(id+"F14.boolean.opBoolean","COPY",FACE,{"derivedFrom":makeQuery(id+"F14.opExtrude","SWEPT_FACE",FACE,{"disambiguationData":[OSD([sQuery(id+"F13.wireOp",EDGE,"E44")])]})});var subQ2=sQuery(id+"F20.wireOp",EDGE,"E64");var subQ3=makeQuery(id+"F21.opExtrude","SWEPT_FACE",FACE,{"disambiguationData":[OSD([subQ2])]});var subQ4=makeQuery(id+"F25.opExtrude","CAP_FACE",FACE,{"disambiguationData":[OSD([sQuery(id+"F24.wireOp",EDGE,"E65"),sQuery(id+"F24.wireOp",EDGE,"E66"),sQuery(id+"F24.wireOp",EDGE,"E67"),sQuery(id+"F24.wireOp",EDGE,"E68"),sQuery(id+"F24.wireOp",EDGE,"E69"),sQuery(id+"F24.wireOp",EDGE,"E70")])],"isStart":true});Q10=makeQuery(id+"F44.opFillet","BLEND_EDGE",EDGE,{"blendedFrom":[makeQuery(id+"F38.boolean.opBoolean","SPLIT",EDGE,{"disambiguationData":[TD([subQ0])],"derivedFrom":makeQuery(id+"F25.boolean.opBoolean","INTERSECT",EDGE,{"derivedFrom":[makeQuery(id+"F21.boolean.opBoolean","SPLIT",FACE,{"disambiguationData":[TD([makeQuery(id+"F1.opExtrude","SWEPT_FACE",FACE,{"disambiguationData":[OSD([sQuery(id+"F0.wireOp",EDGE,"E0.right")])]})])],"derivedFrom":subQ1}),subQ4]})}),makeQuery(id+"F21.boolean.opBoolean","COPY",FACE,{"disambiguationData":[TD([makeQuery(id+"F21.opExtrude","CAP_FACE",FACE,{"disambiguationData":[OSD([subQ2])],"isStart":true})])],"derivedFrom":subQ3})],"blendedInto":[makeQuery(id+"F21.boolean.opBoolean","COPY",FACE,{"disambiguationData":[TD([makeQuery(id+"F21.opExtrude","CAP_FACE",FACE,{"disambiguationData":[OSD([subQ2])],"isStart":true})])],"derivedFrom":subQ3})]});}
            var Q11;
            Q11=makeQuery(id+"F21.boolean.opBoolean","INTERSECT",EDGE,{"disambiguationData":[OD(0.0)],"derivedFrom":[makeQuery(id+"F14.boolean.opBoolean","COPY",FACE,{"derivedFrom":makeQuery(id+"F14.opExtrude","SWEPT_FACE",FACE,{"disambiguationData":[OSD([sQuery(id+"F13.wireOp",EDGE,"E44")])]})}),makeQuery(id+"F21.opExtrude","SWEPT_FACE",FACE,{"disambiguationData":[OSD([sQuery(id+"F20.wireOp",EDGE,"E64")])]})]});
            fillet(context, id + "F45", {"entities" : qUnion([Q0, Q1, Q2, Q3, Q4, Q5, Q6, Q7, Q8, Q9, Q10, Q11]), "radius" : 0.7 * mm, "tangentPropagation" : true});
        }
        {
            var Q0;
            Q0=makeQuery(id+"F21.boolean.opBoolean","INTERSECT",EDGE,{"disambiguationData":[OD(2.0)],"derivedFrom":[makeQuery(id+"F14.boolean.opBoolean","COPY",FACE,{"derivedFrom":makeQuery(id+"F14.opExtrude","SWEPT_FACE",FACE,{"disambiguationData":[OSD([sQuery(id+"F13.wireOp",EDGE,"E44")])]})}),makeQuery(id+"F21.opExtrude","SWEPT_FACE",FACE,{"disambiguationData":[OSD([sQuery(id+"F20.wireOp",EDGE,"E64")])]})]});
            var Q1;
            Q1=makeQuery(id+"F21.boolean.opBoolean","INTERSECT",EDGE,{"disambiguationData":[OD(2.0)],"derivedFrom":[makeQuery(id+"F7.boolean.opBoolean","COPY",FACE,{"derivedFrom":makeQuery(id+"F7.opExtrude","SWEPT_FACE",FACE,{"disambiguationData":[OSD([sQuery(id+"F6.wireOp",EDGE,"E22")])]})}),makeQuery(id+"F21.opExtrude","SWEPT_FACE",FACE,{"disambiguationData":[OSD([sQuery(id+"F20.wireOp",EDGE,"E64")])]})]});
            var Q2;
            Q2=makeQuery(id+"F21.boolean.opBoolean","SPLIT",EDGE,{"disambiguationData":[OD(3.0)],"derivedFrom":makeQuery(id+"F14.boolean.opBoolean","INTERSECT",EDGE,{"derivedFrom":[makeQuery(id+"F7.boolean.opBoolean","COPY",FACE,{"derivedFrom":makeQuery(id+"F7.opExtrude","SWEPT_FACE",FACE,{"disambiguationData":[OSD([sQuery(id+"F6.wireOp",EDGE,"E22")])]})}),makeQuery(id+"F14.opExtrude","SWEPT_FACE",FACE,{"disambiguationData":[OSD([sQuery(id+"F13.wireOp",EDGE,"E44")])]})]})});
            fillet(context, id + "F46", {"entities" : qUnion([Q0, Q1, Q2]), "radius" : 0.3 * mm, "tangentPropagation" : true});
        }
        {
            var Q0;
            Q0=makeQuery(id+"F9.imprint","IMPRINT",FACE,{"disambiguationData":[TD([[makeQuery(id+"F9.imprint","IMPRINT",EDGE,{"derivedFrom":sQuery(id+"F9.wireOp",EDGE,"E42.0")}),1.0]])]});
            var Q1;
            Q1=makeQuery(id+"F9.imprint","IMPRINT",FACE,{"disambiguationData":[TD([[makeQuery(id+"F9.imprint","IMPRINT",EDGE,{"derivedFrom":sQuery(id+"F9.wireOp",EDGE,"E43.1.0")}),-1.0]])]});
            var Q2;
            Q2=makeQuery(id+"F9.imprint","IMPRINT",FACE,{"disambiguationData":[TD([[makeQuery(id+"F9.imprint","IMPRINT",EDGE,{"derivedFrom":sQuery(id+"F9.wireOp",EDGE,"E43.3.0")}),-1.0]])]});
            var Q3;
            Q3=makeQuery(id+"F9.imprint","IMPRINT",FACE,{"disambiguationData":[TD([[makeQuery(id+"F9.imprint","IMPRINT",EDGE,{"derivedFrom":sQuery(id+"F9.wireOp",EDGE,"E43.2.0")}),-1.0]])]});
            extrude(context, id + "F47", {"entities" : qUnion([Q0, Q1, Q2, Q3]), "operationType" : NewBodyOperationType.ADD, "depth" : 5 * mm, "offsetDistance" : 25 * mm});
        }
    });
